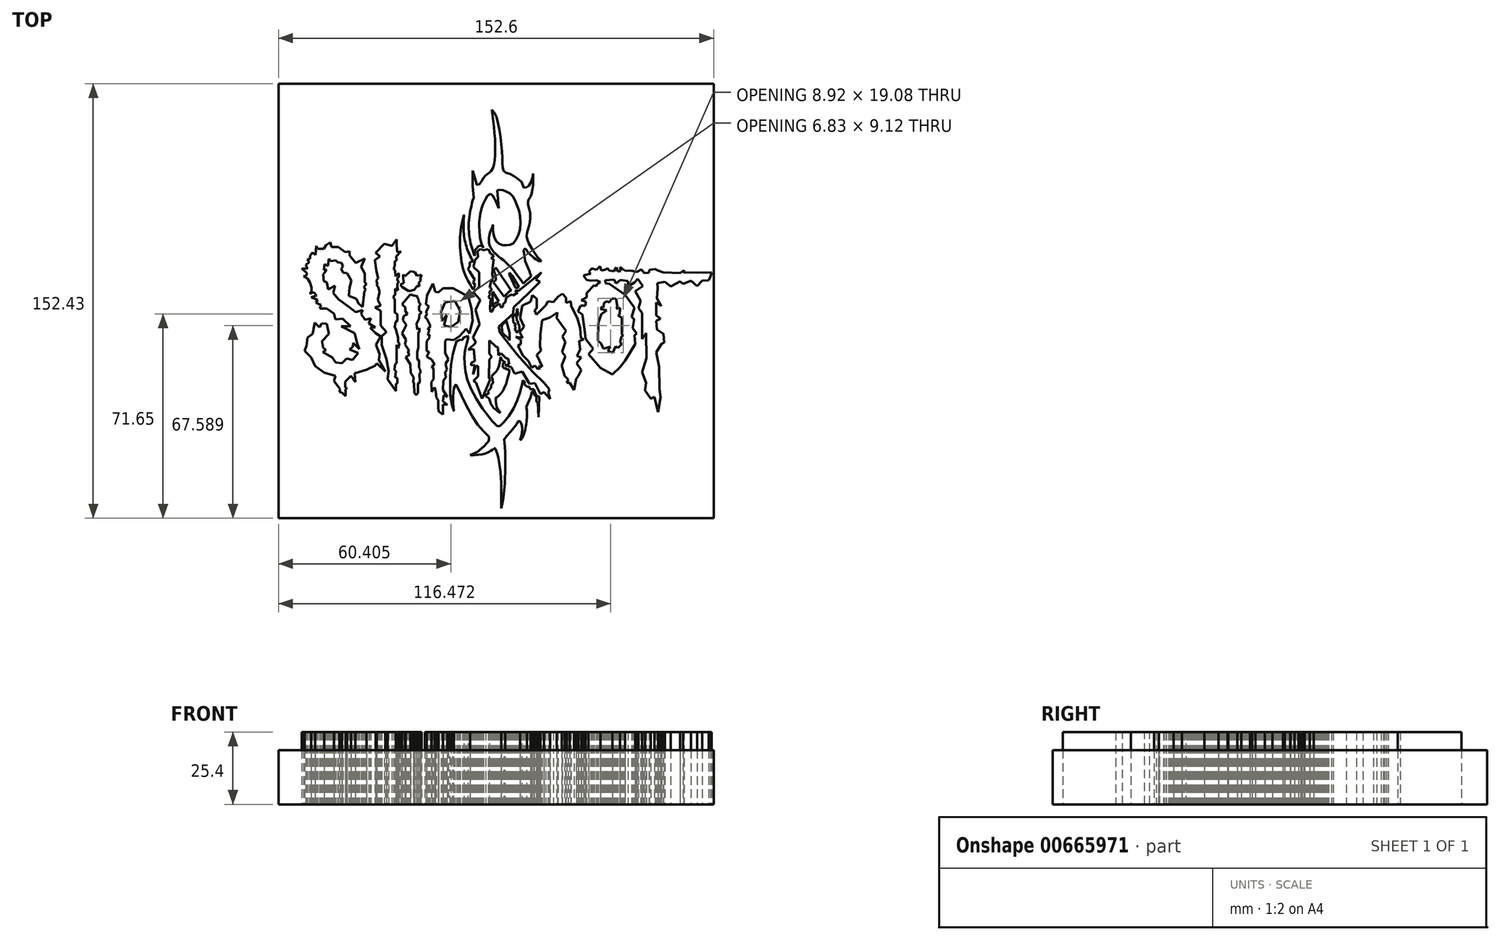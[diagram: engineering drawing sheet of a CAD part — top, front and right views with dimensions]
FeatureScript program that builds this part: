
annotation { "Feature Type Name" : "Feature", "Feature Type Description" : "" }
export const myFeature = defineFeature(function(context is Context, id is Id, definition is map)
    precondition{}
    {
        {
            var Q0;
            Q0=qCreatedBy(makeId("Top.planeOp"),FACE);
            var sketch = newSketch(context, id + "F0", { "sketchPlane" : qUnion([Q0])});
            skLineSegment(sketch, "E0", {"start": v(-46.73, -2.2) * mm, "end": v(-46.31, 1.77) * mm});
            skLineSegment(sketch, "E1", {"start": v(-46.31, 1.77) * mm, "end": v(-46.14, 3.42) * mm});
            skLineSegment(sketch, "E2", {"start": v(-46.14, 3.42) * mm, "end": v(-45.53, 4.04) * mm});
            skLineSegment(sketch, "E3", {"start": v(-45.53, 4.04) * mm, "end": v(-46.31, 4.8) * mm});
            skLineSegment(sketch, "E4", {"start": v(-46.31, 4.8) * mm, "end": v(-45.34, 6) * mm});
            skLineSegment(sketch, "E5", {"start": v(-45.34, 6) * mm, "end": v(-45.93, 6.49) * mm});
            skLineSegment(sketch, "E6", {"start": v(-45.93, 6.49) * mm, "end": v(-45.93, 9.65) * mm});
            skLineSegment(sketch, "E7", {"start": v(-45.93, 9.65) * mm, "end": v(-47.23, 11.97) * mm});
            skLineSegment(sketch, "E8", {"start": v(-47.23, 11.97) * mm, "end": v(-45.93, 14.84) * mm});
            skLineSegment(sketch, "E9", {"start": v(-45.93, 14.84) * mm, "end": v(-49.1, 13.34) * mm});
            skLineSegment(sketch, "E10", {"start": v(-49.1, 13.34) * mm, "end": v(-51.32, 15.98) * mm});
            skLineSegment(sketch, "E11", {"start": v(-51.32, 15.98) * mm, "end": v(-51.32, 17.42) * mm});
            skLineSegment(sketch, "E12", {"start": v(-51.32, 17.42) * mm, "end": v(-52.82, 17.15) * mm});
            skLineSegment(sketch, "E13", {"start": v(-52.82, 17.15) * mm, "end": v(-55.25, 18.95) * mm});
            skLineSegment(sketch, "E14", {"start": v(-55.25, 18.95) * mm, "end": v(-57.6, 18.95) * mm});
            skLineSegment(sketch, "E15", {"start": v(-57.6, 18.95) * mm, "end": v(-58.07, 20.52) * mm});
            skLineSegment(sketch, "E16", {"start": v(-58.07, 20.52) * mm, "end": v(-59.58, 19.6) * mm});
            skLineSegment(sketch, "E17", {"start": v(-59.58, 19.6) * mm, "end": v(-60.29, 18.29) * mm});
            skLineSegment(sketch, "E18", {"start": v(-60.29, 18.29) * mm, "end": v(-62.45, 18.29) * mm});
            skLineSegment(sketch, "E19", {"start": v(-62.45, 18.29) * mm, "end": v(-62.95, 19.34) * mm});
            skLineSegment(sketch, "E20", {"start": v(-62.95, 19.34) * mm, "end": v(-63.28, 16.19) * mm});
            skLineSegment(sketch, "E21", {"start": v(-63.28, 16.19) * mm, "end": v(-64.22, 16.97) * mm});
            skLineSegment(sketch, "E22", {"start": v(-64.22, 16.97) * mm, "end": v(-65.1, 15.9) * mm});
            skLineSegment(sketch, "E23", {"start": v(-65.1, 15.9) * mm, "end": v(-65.1, 14.84) * mm});
            skLineSegment(sketch, "E24", {"start": v(-65.1, 14.84) * mm, "end": v(-66.17, 14.48) * mm});
            skLineSegment(sketch, "E25", {"start": v(-66.17, 14.48) * mm, "end": v(-65.37, 13.68) * mm});
            skLineSegment(sketch, "E26", {"start": v(-65.37, 13.68) * mm, "end": v(-66.7, 12.59) * mm});
            skLineSegment(sketch, "E27", {"start": v(-66.7, 12.59) * mm, "end": v(-66.08, 11.26) * mm});
            skLineSegment(sketch, "E28", {"start": v(-66.08, 11.26) * mm, "end": v(-68.08, 11.47) * mm});
            skLineSegment(sketch, "E29", {"start": v(-68.08, 11.47) * mm, "end": v(-66.33, 9.83) * mm});
            skLineSegment(sketch, "E30", {"start": v(-66.33, 9.83) * mm, "end": v(-66.44, 8.84) * mm});
            skLineSegment(sketch, "E31", {"start": v(-66.44, 8.84) * mm, "end": v(-67.43, 8.67) * mm});
            skLineSegment(sketch, "E32", {"start": v(-67.43, 8.67) * mm, "end": v(-66.06, 7.88) * mm});
            skLineSegment(sketch, "E33", {"start": v(-66.06, 7.88) * mm, "end": v(-65.18, 6.39) * mm});
            skLineSegment(sketch, "E34", {"start": v(-65.18, 6.39) * mm, "end": v(-64.68, 4.65) * mm});
            skLineSegment(sketch, "E35", {"start": v(-64.68, 4.65) * mm, "end": v(-64.68, 3.48) * mm});
            skLineSegment(sketch, "E36", {"start": v(-64.68, 3.48) * mm, "end": v(-65.23, 2.52) * mm});
            skLineSegment(sketch, "E37", {"start": v(-65.23, 2.52) * mm, "end": v(-63.86, 3.09) * mm});
            skLineSegment(sketch, "E38", {"start": v(-63.86, 3.09) * mm, "end": v(-62.82, 1.92) * mm});
            skLineSegment(sketch, "E39", {"start": v(-62.82, 1.92) * mm, "end": v(-64.73, 1.23) * mm});
            skLineSegment(sketch, "E40", {"start": v(-64.73, 1.23) * mm, "end": v(-62.52, 0.39) * mm});
            skLineSegment(sketch, "E41", {"start": v(-62.52, 0.39) * mm, "end": v(-63.09, -0.6) * mm});
            skLineSegment(sketch, "E42", {"start": v(-63.09, -0.6) * mm, "end": v(-61.3, -1.37) * mm});
            skLineSegment(sketch, "E43", {"start": v(-61.3, -1.37) * mm, "end": v(-61.7, -2.69) * mm});
            skLineSegment(sketch, "E44", {"start": v(-61.7, -2.69) * mm, "end": v(-59.24, -2.69) * mm});
            skLineSegment(sketch, "E45", {"start": v(-59.24, -2.69) * mm, "end": v(-56.72, -4.4) * mm});
            skLineSegment(sketch, "E46", {"start": v(-56.72, -4.4) * mm, "end": v(-56.2, -6.44) * mm});
            skLineSegment(sketch, "E47", {"start": v(-56.2, -6.44) * mm, "end": v(-53.75, -6.25) * mm});
            skLineSegment(sketch, "E48", {"start": v(-53.75, -6.25) * mm, "end": v(-50.94, -8.88) * mm});
            skLineSegment(sketch, "E49", {"start": v(-50.94, -8.88) * mm, "end": v(-54.27, -8.88) * mm});
            skLineSegment(sketch, "E50", {"start": v(-54.27, -8.88) * mm, "end": v(-49.54, -11.25) * mm});
            skLineSegment(sketch, "E51", {"start": v(-49.54, -11.25) * mm, "end": v(-48.66, -14.88) * mm});
            skLineSegment(sketch, "E52", {"start": v(-48.66, -14.88) * mm, "end": v(-47.82, -16.95) * mm});
            skLineSegment(sketch, "E53", {"start": v(-47.82, -16.95) * mm, "end": v(-50.04, -14.74) * mm});
            skLineSegment(sketch, "E54", {"start": v(-50.04, -14.74) * mm, "end": v(-50.1, -16.14) * mm});
            skLineSegment(sketch, "E55", {"start": v(-50.1, -16.14) * mm, "end": v(-51.34, -16.98) * mm});
            skLineSegment(sketch, "E56", {"start": v(-51.34, -16.98) * mm, "end": v(-48.2, -18.25) * mm});
            skLineSegment(sketch, "E57", {"start": v(-48.2, -18.25) * mm, "end": v(-50.28, -20.65) * mm});
            skLineSegment(sketch, "E58", {"start": v(-50.28, -20.65) * mm, "end": v(-52.31, -20.2) * mm});
            skLineSegment(sketch, "E59", {"start": v(-52.31, -20.2) * mm, "end": v(-53.9, -21.8) * mm});
            skLineSegment(sketch, "E60", {"start": v(-53.9, -21.8) * mm, "end": v(-56.13, -21.54) * mm});
            skLineSegment(sketch, "E61", {"start": v(-56.13, -21.54) * mm, "end": v(-57.38, -19.8) * mm});
            skLineSegment(sketch, "E62", {"start": v(-57.38, -19.8) * mm, "end": v(-60.63, -17.93) * mm});
            skLineSegment(sketch, "E63", {"start": v(-60.63, -17.93) * mm, "end": v(-59.6, -17.3) * mm});
            skLineSegment(sketch, "E64", {"start": v(-59.6, -17.3) * mm, "end": v(-60.55, -16.38) * mm});
            skLineSegment(sketch, "E65", {"start": v(-60.55, -16.38) * mm, "end": v(-60.95, -14.13) * mm});
            skLineSegment(sketch, "E66", {"start": v(-60.95, -14.13) * mm, "end": v(-58.48, -11.6) * mm});
            skLineSegment(sketch, "E67", {"start": v(-58.48, -11.6) * mm, "end": v(-59.24, -7.98) * mm});
            skLineSegment(sketch, "E68", {"start": v(-59.24, -7.98) * mm, "end": v(-61.08, -7.88) * mm});
            skLineSegment(sketch, "E69", {"start": v(-61.08, -7.88) * mm, "end": v(-61.85, -9.23) * mm});
            skLineSegment(sketch, "E70", {"start": v(-61.85, -9.23) * mm, "end": v(-63.46, -7.66) * mm});
            skLineSegment(sketch, "E71", {"start": v(-63.46, -7.66) * mm, "end": v(-64.2, -11.53) * mm});
            skLineSegment(sketch, "E72", {"start": v(-64.2, -11.53) * mm, "end": v(-66.06, -12.87) * mm});
            skLineSegment(sketch, "E73", {"start": v(-66.06, -12.87) * mm, "end": v(-66.38, -15.81) * mm});
            skLineSegment(sketch, "E74", {"start": v(-66.38, -15.81) * mm, "end": v(-67.09, -17.55) * mm});
            skLineSegment(sketch, "E75", {"start": v(-67.09, -17.55) * mm, "end": v(-64.78, -19.8) * mm});
            skLineSegment(sketch, "E76", {"start": v(-64.78, -19.8) * mm, "end": v(-63.41, -22.83) * mm});
            skLineSegment(sketch, "E77", {"start": v(-63.41, -22.83) * mm, "end": v(-60.23, -25.2) * mm});
            skLineSegment(sketch, "E78", {"start": v(-60.23, -25.2) * mm, "end": v(-56.24, -26.28) * mm});
            skLineSegment(sketch, "E79", {"start": v(-56.24, -26.28) * mm, "end": v(-56.72, -28.03) * mm});
            skLineSegment(sketch, "E80", {"start": v(-56.72, -28.03) * mm, "end": v(-55.48, -29.75) * mm});
            skLineSegment(sketch, "E81", {"start": v(-55.48, -29.75) * mm, "end": v(-54.57, -31.02) * mm});
            skLineSegment(sketch, "E82", {"start": v(-54.57, -31.02) * mm, "end": v(-54.83, -31.95) * mm});
            skLineSegment(sketch, "E83", {"start": v(-54.83, -31.95) * mm, "end": v(-54, -32.17) * mm});
            skLineSegment(sketch, "E84", {"start": v(-54, -32.17) * mm, "end": v(-52.71, -33.43) * mm});
            skLineSegment(sketch, "E85", {"start": v(-52.71, -33.43) * mm, "end": v(-52.71, -31.02) * mm});
            skLineSegment(sketch, "E86", {"start": v(-52.71, -31.02) * mm, "end": v(-52.2, -30.65) * mm});
            skLineSegment(sketch, "E87", {"start": v(-52.2, -30.65) * mm, "end": v(-52.76, -30.4) * mm});
            skLineSegment(sketch, "E88", {"start": v(-52.76, -30.4) * mm, "end": v(-52.76, -28.3) * mm});
            skLineSegment(sketch, "E89", {"start": v(-52.76, -28.3) * mm, "end": v(-50.84, -26.31) * mm});
            skLineSegment(sketch, "E90", {"start": v(-50.84, -26.31) * mm, "end": v(-49.3, -28.47) * mm});
            skLineSegment(sketch, "E91", {"start": v(-49.3, -28.47) * mm, "end": v(-49.54, -25.35) * mm});
            skLineSegment(sketch, "E92", {"start": v(-49.54, -25.35) * mm, "end": v(-45.32, -24.15) * mm});
            skLineSegment(sketch, "E93", {"start": v(-45.32, -24.15) * mm, "end": v(-42.11, -22.56) * mm});
            skLineSegment(sketch, "E94", {"start": v(-42.11, -22.56) * mm, "end": v(-41.72, -21.88) * mm});
            skLineSegment(sketch, "E95", {"start": v(-41.72, -21.88) * mm, "end": v(-38.71, -24.8) * mm});
            skLineSegment(sketch, "E96", {"start": v(-38.71, -24.8) * mm, "end": v(-41, -20.64) * mm});
            skLineSegment(sketch, "E97", {"start": v(-41, -20.64) * mm, "end": v(-40.71, -18.7) * mm});
            skLineSegment(sketch, "E98", {"start": v(-40.71, -18.7) * mm, "end": v(-42.02, -15.33) * mm});
            skLineSegment(sketch, "E99", {"start": v(-42.02, -15.33) * mm, "end": v(-40.34, -12.4) * mm});
            skLineSegment(sketch, "E100", {"start": v(-40.34, -12.4) * mm, "end": v(-42.08, -11.25) * mm});
            skLineSegment(sketch, "E101", {"start": v(-42.08, -11.25) * mm, "end": v(-44.01, -9.36) * mm});
            skLineSegment(sketch, "E102", {"start": v(-44.01, -9.36) * mm, "end": v(-42.32, -9.21) * mm});
            skLineSegment(sketch, "E103", {"start": v(-42.32, -9.21) * mm, "end": v(-44.6, -7.9) * mm});
            skLineSegment(sketch, "E104", {"start": v(-44.6, -7.9) * mm, "end": v(-43.86, -6.08) * mm});
            skLineSegment(sketch, "E105", {"start": v(-43.86, -6.08) * mm, "end": v(-45.78, -6.6) * mm});
            skLineSegment(sketch, "E106", {"start": v(-45.78, -6.6) * mm, "end": v(-47.27, -4.53) * mm});
            skLineSegment(sketch, "E107", {"start": v(-47.27, -4.53) * mm, "end": v(-46.72, -3.17) * mm});
            skLineSegment(sketch, "E108", {"start": v(-46.72, -3.17) * mm, "end": v(-49.14, -3.92) * mm});
            skLineSegment(sketch, "E109", {"start": v(-49.14, -3.92) * mm, "end": v(-51.42, -2.14) * mm});
            skLineSegment(sketch, "E110", {"start": v(-51.42, -2.14) * mm, "end": v(-55.25, 0.63) * mm});
            skLineSegment(sketch, "E111", {"start": v(-55.25, 0.63) * mm, "end": v(-57.06, 2.73) * mm});
            skLineSegment(sketch, "E112", {"start": v(-57.06, 2.73) * mm, "end": v(-56.34, 5.4) * mm});
            skLineSegment(sketch, "E113", {"start": v(-56.34, 5.4) * mm, "end": v(-58.78, 4.1) * mm});
            skLineSegment(sketch, "E114", {"start": v(-58.78, 4.1) * mm, "end": v(-59.24, 6.57) * mm});
            skLineSegment(sketch, "E115", {"start": v(-59.24, 6.57) * mm, "end": v(-60.3, 6.86) * mm});
            skLineSegment(sketch, "E116", {"start": v(-60.3, 6.86) * mm, "end": v(-60.55, 9.24) * mm});
            skLineSegment(sketch, "E117", {"start": v(-60.55, 9.24) * mm, "end": v(-59.24, 10.93) * mm});
            skLineSegment(sketch, "E118", {"start": v(-59.24, 10.93) * mm, "end": v(-60.35, 10.93) * mm});
            skLineSegment(sketch, "E119", {"start": v(-60.35, 10.93) * mm, "end": v(-60.04, 13) * mm});
            skLineSegment(sketch, "E120", {"start": v(-60.04, 13) * mm, "end": v(-58.9, 12.25) * mm});
            skLineSegment(sketch, "E121", {"start": v(-58.9, 12.25) * mm, "end": v(-58.52, 14.8) * mm});
            skLineSegment(sketch, "E122", {"start": v(-58.52, 14.8) * mm, "end": v(-57.95, 14.01) * mm});
            skLineSegment(sketch, "E123", {"start": v(-57.95, 14.01) * mm, "end": v(-56.17, 14.27) * mm});
            skLineSegment(sketch, "E124", {"start": v(-56.17, 14.27) * mm, "end": v(-55.48, 13.6) * mm});
            skLineSegment(sketch, "E125", {"start": v(-55.48, 13.6) * mm, "end": v(-54.05, 13.38) * mm});
            skLineSegment(sketch, "E126", {"start": v(-54.05, 13.38) * mm, "end": v(-53.52, 12) * mm});
            skLineSegment(sketch, "E127", {"start": v(-53.52, 12) * mm, "end": v(-54.26, 11.24) * mm});
            skLineSegment(sketch, "E128", {"start": v(-54.26, 11.24) * mm, "end": v(-53.56, 9.96) * mm});
            skLineSegment(sketch, "E129", {"start": v(-53.56, 9.96) * mm, "end": v(-52.22, 9.76) * mm});
            skLineSegment(sketch, "E130", {"start": v(-52.22, 9.76) * mm, "end": v(-50.7, 7.1) * mm});
            skLineSegment(sketch, "E131", {"start": v(-50.7, 7.1) * mm, "end": v(-51.33, 4.74) * mm});
            skLineSegment(sketch, "E132", {"start": v(-51.33, 4.74) * mm, "end": v(-51.48, 1.75) * mm});
            skLineSegment(sketch, "E133", {"start": v(-51.48, 1.75) * mm, "end": v(-48.93, 0.71) * mm});
            skLineSegment(sketch, "E134", {"start": v(-48.93, 0.71) * mm, "end": v(-48.21, -0.75) * mm});
            skLineSegment(sketch, "E135", {"start": v(-48.21, -0.75) * mm, "end": v(-46.73, -2.2) * mm});
            skPoint(sketch, "E136.end.orphan", {"position": v(-38.71, 15.6) * mm});
            skLineSegment(sketch, "E137", {"start": v(-34.72, 21.53) * mm, "end": v(-36.49, 19.25) * mm});
            skLineSegment(sketch, "E138", {"start": v(-36.49, 19.25) * mm, "end": v(-39.07, 20.12) * mm});
            skLineSegment(sketch, "E139", {"start": v(-39.07, 20.12) * mm, "end": v(-42.1, 16.94) * mm});
            skLineSegment(sketch, "E140", {"start": v(-42.1, 16.94) * mm, "end": v(-40.65, 15.57) * mm});
            skLineSegment(sketch, "E141", {"start": v(-40.65, 15.57) * mm, "end": v(-42.37, 14.39) * mm});
            skLineSegment(sketch, "E142", {"start": v(-42.37, 14.39) * mm, "end": v(-41.93, 10.72) * mm});
            skLineSegment(sketch, "E143", {"start": v(-41.93, 10.72) * mm, "end": v(-41.3, 7.92) * mm});
            skLineSegment(sketch, "E144", {"start": v(-41.3, 7.92) * mm, "end": v(-42.03, 6.97) * mm});
            skLineSegment(sketch, "E145", {"start": v(-42.03, 6.97) * mm, "end": v(-41.32, 6.12) * mm});
            skLineSegment(sketch, "E146", {"start": v(-41.32, 6.12) * mm, "end": v(-41.83, 5.7) * mm});
            skLineSegment(sketch, "E147", {"start": v(-41.83, 5.7) * mm, "end": v(-41.19, 4.93) * mm});
            skLineSegment(sketch, "E148", {"start": v(-41.19, 4.93) * mm, "end": v(-40.71, 3.12) * mm});
            skLineSegment(sketch, "E149", {"start": v(-40.71, 3.12) * mm, "end": v(-41.4, 0.32) * mm});
            skLineSegment(sketch, "E150", {"start": v(-41.4, 0.32) * mm, "end": v(-40.32, -1.68) * mm});
            skLineSegment(sketch, "E151", {"start": v(-40.32, -1.68) * mm, "end": v(-42.44, -2.34) * mm});
            skLineSegment(sketch, "E152", {"start": v(-42.44, -2.34) * mm, "end": v(-40.32, -3.44) * mm});
            skLineSegment(sketch, "E153", {"start": v(-40.32, -3.44) * mm, "end": v(-40.32, -8.64) * mm});
            skLineSegment(sketch, "E154", {"start": v(-40.32, -8.64) * mm, "end": v(-38.29, -10.9) * mm});
            skLineSegment(sketch, "E155", {"start": v(-38.29, -10.9) * mm, "end": v(-39.92, -12.36) * mm});
            skLineSegment(sketch, "E156", {"start": v(-39.92, -12.36) * mm, "end": v(-39.92, -15.52) * mm});
            skLineSegment(sketch, "E157", {"start": v(-39.92, -15.52) * mm, "end": v(-38.33, -20.4) * mm});
            skLineSegment(sketch, "E158", {"start": v(-38.33, -20.4) * mm, "end": v(-37.61, -24.6) * mm});
            skLineSegment(sketch, "E159", {"start": v(-37.61, -24.6) * mm, "end": v(-37.89, -27.38) * mm});
            skLineSegment(sketch, "E160", {"start": v(-37.89, -27.38) * mm, "end": v(-35, -31.58) * mm});
            skLineSegment(sketch, "E161", {"start": v(-35, -31.58) * mm, "end": v(-35, -29.16) * mm});
            skLineSegment(sketch, "E162", {"start": v(-35, -29.16) * mm, "end": v(-34.46, -28.86) * mm});
            skLineSegment(sketch, "E163", {"start": v(-34.46, -28.86) * mm, "end": v(-34.46, -27.04) * mm});
            skLineSegment(sketch, "E164", {"start": v(-34.46, -27.04) * mm, "end": v(-35.21, -26.85) * mm});
            skLineSegment(sketch, "E165", {"start": v(-35.21, -26.85) * mm, "end": v(-34.99, -24.58) * mm});
            skLineSegment(sketch, "E166", {"start": v(-34.99, -24.58) * mm, "end": v(-35.49, -24.1) * mm});
            skLineSegment(sketch, "E167", {"start": v(-35.49, -24.1) * mm, "end": v(-35.3, -22.1) * mm});
            skLineSegment(sketch, "E168", {"start": v(-35.3, -22.1) * mm, "end": v(-34.76, -21.8) * mm});
            skLineSegment(sketch, "E169", {"start": v(-34.76, -21.8) * mm, "end": v(-34.76, -15.73) * mm});
            skLineSegment(sketch, "E170", {"start": v(-34.76, -15.73) * mm, "end": v(-34.66, -15.3) * mm});
            skLineSegment(sketch, "E171", {"start": v(-34.66, -15.3) * mm, "end": v(-34.26, -16.66) * mm});
            skLineSegment(sketch, "E172", {"start": v(-34.26, -16.66) * mm, "end": v(-33.8, -14.86) * mm});
            skLineSegment(sketch, "E173", {"start": v(-33.8, -14.86) * mm, "end": v(-34.32, -14.46) * mm});
            skLineSegment(sketch, "E174", {"start": v(-34.32, -14.46) * mm, "end": v(-34.32, -12.85) * mm});
            skLineSegment(sketch, "E175", {"start": v(-34.32, -12.85) * mm, "end": v(-35.04, -10.03) * mm});
            skLineSegment(sketch, "E176", {"start": v(-35.04, -10.03) * mm, "end": v(-35.38, -9.18) * mm});
            skLineSegment(sketch, "E177", {"start": v(-35.38, -9.18) * mm, "end": v(-35.2, -7.33) * mm});
            skLineSegment(sketch, "E178", {"start": v(-35.2, -7.33) * mm, "end": v(-34.58, -7.03) * mm});
            skLineSegment(sketch, "E179", {"start": v(-34.58, -7.03) * mm, "end": v(-34.58, -4.68) * mm});
            skLineSegment(sketch, "E180", {"start": v(-34.58, -4.68) * mm, "end": v(-35.45, -4.1) * mm});
            skLineSegment(sketch, "E181", {"start": v(-35.45, -4.1) * mm, "end": v(-35.45, 0.62) * mm});
            skLineSegment(sketch, "E182", {"start": v(-35.45, 0.62) * mm, "end": v(-35.82, 0.88) * mm});
            skLineSegment(sketch, "E183", {"start": v(-35.82, 0.88) * mm, "end": v(-35.77, 1.82) * mm});
            skLineSegment(sketch, "E184", {"start": v(-35.77, 1.82) * mm, "end": v(-35.34, 2.15) * mm});
            skLineSegment(sketch, "E185", {"start": v(-35.34, 2.15) * mm, "end": v(-35.34, 4.27) * mm});
            skLineSegment(sketch, "E186", {"start": v(-35.34, 4.27) * mm, "end": v(-34.29, 3.72) * mm});
            skLineSegment(sketch, "E187", {"start": v(-34.29, 3.72) * mm, "end": v(-34.58, 4.93) * mm});
            skLineSegment(sketch, "E188", {"start": v(-34.58, 4.93) * mm, "end": v(-34.58, 6.14) * mm});
            skLineSegment(sketch, "E189", {"start": v(-34.58, 6.14) * mm, "end": v(-34.18, 6.53) * mm});
            skLineSegment(sketch, "E190", {"start": v(-34.18, 6.53) * mm, "end": v(-34.04, 7) * mm});
            skLineSegment(sketch, "E191", {"start": v(-34.04, 7) * mm, "end": v(-34.58, 7.05) * mm});
            skLineSegment(sketch, "E192", {"start": v(-34.58, 7.05) * mm, "end": v(-34.58, 8.05) * mm});
            skLineSegment(sketch, "E193", {"start": v(-34.58, 8.05) * mm, "end": v(-33.96, 8.32) * mm});
            skLineSegment(sketch, "E194", {"start": v(-33.96, 8.32) * mm, "end": v(-33.96, 9.83) * mm});
            skLineSegment(sketch, "E195", {"start": v(-33.96, 9.83) * mm, "end": v(-35.1, 8.66) * mm});
            skLineSegment(sketch, "E196", {"start": v(-35.1, 8.66) * mm, "end": v(-35.32, 10.67) * mm});
            skLineSegment(sketch, "E197", {"start": v(-35.32, 10.67) * mm, "end": v(-35.71, 10.94) * mm});
            skLineSegment(sketch, "E198", {"start": v(-35.71, 10.94) * mm, "end": v(-35.71, 11.88) * mm});
            skLineSegment(sketch, "E199", {"start": v(-35.71, 11.88) * mm, "end": v(-35.4, 12.15) * mm});
            skLineSegment(sketch, "E200", {"start": v(-35.4, 12.15) * mm, "end": v(-35.4, 13.97) * mm});
            skLineSegment(sketch, "E201", {"start": v(-35.4, 13.97) * mm, "end": v(-34.82, 14.28) * mm});
            skLineSegment(sketch, "E202", {"start": v(-34.82, 14.28) * mm, "end": v(-34.9, 15.6) * mm});
            skLineSegment(sketch, "E203", {"start": v(-34.9, 15.6) * mm, "end": v(-33.23, 17.41) * mm});
            skLineSegment(sketch, "E204", {"start": v(-33.23, 17.41) * mm, "end": v(-34.58, 17.08) * mm});
            skLineSegment(sketch, "E205", {"start": v(-34.58, 17.08) * mm, "end": v(-34.77, 19.41) * mm});
            skLineSegment(sketch, "E206", {"start": v(-34.77, 19.41) * mm, "end": v(-34.72, 21.53) * mm});
            skLineSegment(sketch, "E207", {"start": v(-29.97, 10.44) * mm, "end": v(-31.9, 8.58) * mm});
            skLineSegment(sketch, "E208", {"start": v(-31.9, 8.58) * mm, "end": v(-32.52, 9.22) * mm});
            skLineSegment(sketch, "E209", {"start": v(-32.52, 9.22) * mm, "end": v(-32.52, 7.9) * mm});
            skLineSegment(sketch, "E210", {"start": v(-32.52, 7.9) * mm, "end": v(-32.24, 6.37) * mm});
            skLineSegment(sketch, "E211", {"start": v(-32.24, 6.37) * mm, "end": v(-33.5, 5.68) * mm});
            skLineSegment(sketch, "E212", {"start": v(-33.5, 5.68) * mm, "end": v(-32.7, 4.8) * mm});
            skLineSegment(sketch, "E213", {"start": v(-32.7, 4.8) * mm, "end": v(-30.48, 3.44) * mm});
            skLineSegment(sketch, "E214", {"start": v(-30.48, 3.44) * mm, "end": v(-28.61, 3.98) * mm});
            skLineSegment(sketch, "E215", {"start": v(-28.61, 3.98) * mm, "end": v(-27.51, 5.39) * mm});
            skLineSegment(sketch, "E216", {"start": v(-27.51, 5.39) * mm, "end": v(-26.72, 5.08) * mm});
            skLineSegment(sketch, "E217", {"start": v(-26.72, 5.08) * mm, "end": v(-27.06, 6.5) * mm});
            skLineSegment(sketch, "E218", {"start": v(-27.06, 6.5) * mm, "end": v(-26.32, 7.16) * mm});
            skLineSegment(sketch, "E219", {"start": v(-26.32, 7.16) * mm, "end": v(-26.51, 7.8) * mm});
            skLineSegment(sketch, "E220", {"start": v(-26.51, 7.8) * mm, "end": v(-26, 9.09) * mm});
            skLineSegment(sketch, "E221", {"start": v(-26, 9.09) * mm, "end": v(-27.72, 8.83) * mm});
            skLineSegment(sketch, "E222", {"start": v(-27.72, 8.83) * mm, "end": v(-28.41, 10.1) * mm});
            skLineSegment(sketch, "E223", {"start": v(-28.41, 10.1) * mm, "end": v(-29.97, 10.44) * mm});
            skLineSegment(sketch, "E224", {"start": v(-29.97, 2.3) * mm, "end": v(-32.85, -1.12) * mm});
            skLineSegment(sketch, "E225", {"start": v(-32.85, -1.12) * mm, "end": v(-31.6, -2.47) * mm});
            skLineSegment(sketch, "E226", {"start": v(-31.6, -2.47) * mm, "end": v(-31.83, -3.3) * mm});
            skLineSegment(sketch, "E227", {"start": v(-31.83, -3.3) * mm, "end": v(-30.92, -4.74) * mm});
            skLineSegment(sketch, "E228", {"start": v(-30.92, -4.74) * mm, "end": v(-32.17, -5.23) * mm});
            skLineSegment(sketch, "E229", {"start": v(-32.17, -5.23) * mm, "end": v(-32.56, -6.72) * mm});
            skLineSegment(sketch, "E230", {"start": v(-32.56, -6.72) * mm, "end": v(-31.37, -8.4) * mm});
            skLineSegment(sketch, "E231", {"start": v(-31.37, -8.4) * mm, "end": v(-32.85, -11.38) * mm});
            skLineSegment(sketch, "E232", {"start": v(-32.85, -11.38) * mm, "end": v(-31.41, -13.63) * mm});
            skLineSegment(sketch, "E233", {"start": v(-31.41, -13.63) * mm, "end": v(-31.81, -15.26) * mm});
            skLineSegment(sketch, "E234", {"start": v(-31.81, -15.26) * mm, "end": v(-30.82, -16.75) * mm});
            skLineSegment(sketch, "E235", {"start": v(-30.82, -16.75) * mm, "end": v(-30.29, -17.58) * mm});
            skLineSegment(sketch, "E236", {"start": v(-30.29, -17.58) * mm, "end": v(-31, -17.85) * mm});
            skLineSegment(sketch, "E237", {"start": v(-31, -17.85) * mm, "end": v(-30.24, -18.95) * mm});
            skLineSegment(sketch, "E238", {"start": v(-30.24, -18.95) * mm, "end": v(-31.6, -19.7) * mm});
            skLineSegment(sketch, "E239", {"start": v(-31.6, -19.7) * mm, "end": v(-29.91, -22.25) * mm});
            skLineSegment(sketch, "E240", {"start": v(-29.91, -22.25) * mm, "end": v(-29.86, -25.23) * mm});
            skLineSegment(sketch, "E241", {"start": v(-29.86, -25.23) * mm, "end": v(-28.86, -26.77) * mm});
            skLineSegment(sketch, "E242", {"start": v(-28.86, -26.77) * mm, "end": v(-28.95, -28.39) * mm});
            skLineSegment(sketch, "E243", {"start": v(-28.95, -28.39) * mm, "end": v(-28.63, -29.02) * mm});
            skLineSegment(sketch, "E244", {"start": v(-28.63, -29.02) * mm, "end": v(-28.61, -32.27) * mm});
            skLineSegment(sketch, "E245", {"start": v(-28.61, -32.27) * mm, "end": v(-27.86, -32.98) * mm});
            skLineSegment(sketch, "E246", {"start": v(-27.86, -32.98) * mm, "end": v(-27.24, -32.3) * mm});
            skLineSegment(sketch, "E247", {"start": v(-27.24, -32.3) * mm, "end": v(-27.35, -28.9) * mm});
            skLineSegment(sketch, "E248", {"start": v(-27.35, -28.9) * mm, "end": v(-26.7, -28.54) * mm});
            skLineSegment(sketch, "E249", {"start": v(-26.7, -28.54) * mm, "end": v(-26.84, -25.48) * mm});
            skLineSegment(sketch, "E250", {"start": v(-26.84, -25.48) * mm, "end": v(-26.45, -25.14) * mm});
            skLineSegment(sketch, "E251", {"start": v(-26.45, -25.14) * mm, "end": v(-26.5, -24) * mm});
            skLineSegment(sketch, "E252", {"start": v(-26.5, -24) * mm, "end": v(-26.94, -23.5) * mm});
            skLineSegment(sketch, "E253", {"start": v(-26.94, -23.5) * mm, "end": v(-26.88, -20.83) * mm});
            skLineSegment(sketch, "E254", {"start": v(-26.88, -20.83) * mm, "end": v(-27.59, -20.43) * mm});
            skLineSegment(sketch, "E255", {"start": v(-27.59, -20.43) * mm, "end": v(-27.48, -17.9) * mm});
            skLineSegment(sketch, "E256", {"start": v(-27.48, -17.9) * mm, "end": v(-27.15, -16.33) * mm});
            skLineSegment(sketch, "E257", {"start": v(-27.15, -16.33) * mm, "end": v(-27.21, -13.78) * mm});
            skLineSegment(sketch, "E258", {"start": v(-27.21, -13.78) * mm, "end": v(-27.21, -11.47) * mm});
            skLineSegment(sketch, "E259", {"start": v(-27.21, -11.47) * mm, "end": v(-26.8, -10.54) * mm});
            skLineSegment(sketch, "E260", {"start": v(-26.8, -10.54) * mm, "end": v(-26.82, -9.58) * mm});
            skLineSegment(sketch, "E261", {"start": v(-26.82, -9.58) * mm, "end": v(-27.56, -10) * mm});
            skLineSegment(sketch, "E262", {"start": v(-27.56, -10) * mm, "end": v(-27.81, -7.96) * mm});
            skLineSegment(sketch, "E263", {"start": v(-27.81, -7.96) * mm, "end": v(-26.87, -6.21) * mm});
            skLineSegment(sketch, "E264", {"start": v(-26.87, -6.21) * mm, "end": v(-26.82, -4.7) * mm});
            skLineSegment(sketch, "E265", {"start": v(-26.82, -4.7) * mm, "end": v(-26.02, -4.02) * mm});
            skLineSegment(sketch, "E266", {"start": v(-26.02, -4.02) * mm, "end": v(-26.95, -3.36) * mm});
            skLineSegment(sketch, "E267", {"start": v(-26.95, -3.36) * mm, "end": v(-26.95, -1.83) * mm});
            skLineSegment(sketch, "E268", {"start": v(-26.95, -1.83) * mm, "end": v(-26.42, -1.46) * mm});
            skLineSegment(sketch, "E269", {"start": v(-26.42, -1.46) * mm, "end": v(-26.52, -0.91) * mm});
            skLineSegment(sketch, "E270", {"start": v(-26.52, -0.91) * mm, "end": v(-26.96, -0.76) * mm});
            skLineSegment(sketch, "E271", {"start": v(-26.96, -0.76) * mm, "end": v(-27.11, 0.7) * mm});
            skLineSegment(sketch, "E272", {"start": v(-27.11, 0.7) * mm, "end": v(-27.55, 1.04) * mm});
            skLineSegment(sketch, "E273", {"start": v(-27.55, 1.04) * mm, "end": v(-27.35, 1.63) * mm});
            skLineSegment(sketch, "E274", {"start": v(-27.35, 1.63) * mm, "end": v(-28.85, 1.96) * mm});
            skLineSegment(sketch, "E275", {"start": v(-28.85, 1.96) * mm, "end": v(-29.97, 2.3) * mm});
            skLineSegment(sketch, "E276", {"start": v(-22.02, 6.06) * mm, "end": v(-24.12, 1.92) * mm});
            skLineSegment(sketch, "E277", {"start": v(-24.12, 1.92) * mm, "end": v(-24.43, -1.17) * mm});
            skLineSegment(sketch, "E278", {"start": v(-24.43, -1.17) * mm, "end": v(-23.48, -1.88) * mm});
            skLineSegment(sketch, "E279", {"start": v(-23.48, -1.88) * mm, "end": v(-24.32, -3.66) * mm});
            skLineSegment(sketch, "E280", {"start": v(-24.32, -3.66) * mm, "end": v(-24.18, -5) * mm});
            skLineSegment(sketch, "E281", {"start": v(-24.18, -5) * mm, "end": v(-24.86, -5.6) * mm});
            skLineSegment(sketch, "E282", {"start": v(-24.86, -5.6) * mm, "end": v(-24.1, -6.4) * mm});
            skLineSegment(sketch, "E283", {"start": v(-24.1, -6.4) * mm, "end": v(-23.04, -8.34) * mm});
            skLineSegment(sketch, "E284", {"start": v(-23.04, -8.34) * mm, "end": v(-23.07, -9.38) * mm});
            skLineSegment(sketch, "E285", {"start": v(-23.07, -9.38) * mm, "end": v(-23.9, -9.53) * mm});
            skLineSegment(sketch, "E286", {"start": v(-23.9, -9.53) * mm, "end": v(-23.19, -10.57) * mm});
            skLineSegment(sketch, "E287", {"start": v(-23.19, -10.57) * mm, "end": v(-23.82, -11.3) * mm});
            skLineSegment(sketch, "E288", {"start": v(-23.82, -11.3) * mm, "end": v(-23.13, -12.6) * mm});
            skLineSegment(sketch, "E289", {"start": v(-23.13, -12.6) * mm, "end": v(-24.22, -14.21) * mm});
            skLineSegment(sketch, "E290", {"start": v(-24.22, -14.21) * mm, "end": v(-24.22, -17.7) * mm});
            skLineSegment(sketch, "E291", {"start": v(-24.22, -17.7) * mm, "end": v(-23.3, -17.78) * mm});
            skLineSegment(sketch, "E292", {"start": v(-23.3, -17.78) * mm, "end": v(-24.24, -19.56) * mm});
            skLineSegment(sketch, "E293", {"start": v(-24.24, -19.56) * mm, "end": v(-22.44, -20.6) * mm});
            skLineSegment(sketch, "E294", {"start": v(-22.44, -20.6) * mm, "end": v(-21.4, -22.32) * mm});
            skLineSegment(sketch, "E295", {"start": v(-21.4, -22.32) * mm, "end": v(-22.47, -22.88) * mm});
            skLineSegment(sketch, "E296", {"start": v(-22.47, -22.88) * mm, "end": v(-21.79, -23.83) * mm});
            skLineSegment(sketch, "E297", {"start": v(-21.79, -23.83) * mm, "end": v(-21.79, -27.38) * mm});
            skLineSegment(sketch, "E298", {"start": v(-21.79, -27.38) * mm, "end": v(-22.63, -28.46) * mm});
            skLineSegment(sketch, "E299", {"start": v(-22.63, -28.46) * mm, "end": v(-22.42, -31.9) * mm});
            skLineSegment(sketch, "E300", {"start": v(-22.42, -31.9) * mm, "end": v(-21.48, -30.32) * mm});
            skLineSegment(sketch, "E301", {"start": v(-21.48, -30.32) * mm, "end": v(-21.1, -31.7) * mm});
            skLineSegment(sketch, "E302", {"start": v(-21.1, -31.7) * mm, "end": v(-20.86, -34.03) * mm});
            skLineSegment(sketch, "E303", {"start": v(-20.86, -34.03) * mm, "end": v(-20.15, -34.76) * mm});
            skLineSegment(sketch, "E304", {"start": v(-20.15, -34.76) * mm, "end": v(-20.15, -37.36) * mm});
            skLineSegment(sketch, "E305", {"start": v(-20.15, -37.36) * mm, "end": v(-20, -38.73) * mm});
            skLineSegment(sketch, "E306", {"start": v(-20, -38.73) * mm, "end": v(-18.5, -39.9) * mm});
            skLineSegment(sketch, "E307", {"start": v(-18.5, -39.9) * mm, "end": v(-18.5, -36.32) * mm});
            skLineSegment(sketch, "E308", {"start": v(-18.5, -36.32) * mm, "end": v(-17.03, -36.47) * mm});
            skLineSegment(sketch, "E309", {"start": v(-17.03, -36.47) * mm, "end": v(-18.5, -35.14) * mm});
            skLineSegment(sketch, "E310", {"start": v(-18.5, -35.14) * mm, "end": v(-18.26, -33.07) * mm});
            skLineSegment(sketch, "E311", {"start": v(-18.26, -33.07) * mm, "end": v(-16.97, -33.6) * mm});
            skLineSegment(sketch, "E312", {"start": v(-16.97, -33.6) * mm, "end": v(-18.5, -31.29) * mm});
            skLineSegment(sketch, "E313", {"start": v(-18.5, -31.29) * mm, "end": v(-18.36, -27.93) * mm});
            skLineSegment(sketch, "E314", {"start": v(-18.36, -27.93) * mm, "end": v(-17.5, -26.84) * mm});
            skLineSegment(sketch, "E315", {"start": v(-17.5, -26.84) * mm, "end": v(-17.73, -24.97) * mm});
            skLineSegment(sketch, "E316", {"start": v(-17.73, -24.97) * mm, "end": v(-17.18, -24.19) * mm});
            skLineSegment(sketch, "E317", {"start": v(-17.18, -24.19) * mm, "end": v(-17.68, -22.12) * mm});
            skLineSegment(sketch, "E318", {"start": v(-17.68, -22.12) * mm, "end": v(-16.65, -20.4) * mm});
            skLineSegment(sketch, "E319", {"start": v(-16.65, -20.4) * mm, "end": v(-17.78, -18.32) * mm});
            skLineSegment(sketch, "E320", {"start": v(-17.78, -18.32) * mm, "end": v(-17.78, -14.13) * mm});
            skLineSegment(sketch, "E321", {"start": v(-17.78, -14.13) * mm, "end": v(-17.25, -13.46) * mm});
            skLineSegment(sketch, "E322", {"start": v(-17.25, -13.46) * mm, "end": v(-14.71, -13.71) * mm});
            skLineSegment(sketch, "E323", {"start": v(-14.71, -13.71) * mm, "end": v(-12.69, -12.35) * mm});
            skLineSegment(sketch, "E324", {"start": v(-12.69, -12.35) * mm, "end": v(-10.4, -9.78) * mm});
            skLineSegment(sketch, "E325", {"start": v(-10.4, -9.78) * mm, "end": v(-9.26, -11.38) * mm});
            skLineSegment(sketch, "E326", {"start": v(-9.26, -11.38) * mm, "end": v(-8.14, -7.03) * mm});
            skLineSegment(sketch, "E327", {"start": v(-8.14, -7.03) * mm, "end": v(-8.55, -2.82) * mm});
            skLineSegment(sketch, "E328", {"start": v(-8.55, -2.82) * mm, "end": v(-9.58, 1.57) * mm});
            skLineSegment(sketch, "E329", {"start": v(-9.58, 1.57) * mm, "end": v(-15, 4.5) * mm});
            skLineSegment(sketch, "E330", {"start": v(-15, 4.5) * mm, "end": v(-18.5, 4.5) * mm});
            skLineSegment(sketch, "E331", {"start": v(-18.5, 4.5) * mm, "end": v(-20.04, 3.07) * mm});
            skLineSegment(sketch, "E332", {"start": v(-20.04, 3.07) * mm, "end": v(-21.2, 3.18) * mm});
            skLineSegment(sketch, "E333", {"start": v(-21.2, 3.18) * mm, "end": v(-22.02, 6.06) * mm});
            skLineSegment(sketch, "E334", {"start": v(-15.67, -9.12) * mm, "end": v(-13.15, -7.33) * mm});
            skLineSegment(sketch, "E335", {"start": v(-13.15, -7.33) * mm, "end": v(-12.36, -3.56) * mm});
            skLineSegment(sketch, "E336", {"start": v(-12.36, -3.56) * mm, "end": v(-14.3, 0) * mm});
            skLineSegment(sketch, "E337", {"start": v(-14.3, 0) * mm, "end": v(-17.75, -0.47) * mm});
            skLineSegment(sketch, "E338", {"start": v(-17.75, -0.47) * mm, "end": v(-19.19, -3.73) * mm});
            skLineSegment(sketch, "E339", {"start": v(-19.19, -3.73) * mm, "end": v(-18.85, -7.03) * mm});
            skLineSegment(sketch, "E340", {"start": v(-18.85, -7.03) * mm, "end": v(-17.24, -4.96) * mm});
            skLineSegment(sketch, "E341", {"start": v(-17.24, -4.96) * mm, "end": v(-18.18, -8.6) * mm});
            skLineSegment(sketch, "E342", {"start": v(-18.18, -8.6) * mm, "end": v(-15.67, -9.12) * mm});
            skLineSegment(sketch, "E343", {"start": v(-5.3, 18.28) * mm, "end": v(-6.44, 17.35) * mm});
            skLineSegment(sketch, "E344", {"start": v(-6.44, 17.35) * mm, "end": v(-6.25, 15.5) * mm});
            skLineSegment(sketch, "E345", {"start": v(-6.25, 15.5) * mm, "end": v(-7.18, 14.5) * mm});
            skLineSegment(sketch, "E346", {"start": v(-7.18, 14.5) * mm, "end": v(-7.84, 11.96) * mm});
            skLineSegment(sketch, "E347", {"start": v(-7.84, 11.96) * mm, "end": v(-5.81, 10.04) * mm});
            skLineSegment(sketch, "E348", {"start": v(-5.81, 10.04) * mm, "end": v(-5.81, 4.93) * mm});
            skLineSegment(sketch, "E349", {"start": v(-5.81, 4.93) * mm, "end": v(-7.88, 3) * mm});
            skLineSegment(sketch, "E350", {"start": v(-7.88, 3) * mm, "end": v(-5.44, 0.38) * mm});
            skLineSegment(sketch, "E351", {"start": v(-5.44, 0.38) * mm, "end": v(-7.13, -3.2) * mm});
            skLineSegment(sketch, "E352", {"start": v(-7.13, -3.2) * mm, "end": v(-5.67, -8.12) * mm});
            skLineSegment(sketch, "E353", {"start": v(-5.67, -8.12) * mm, "end": v(-7.99, -12.8) * mm});
            skLineSegment(sketch, "E354", {"start": v(-7.99, -12.8) * mm, "end": v(-7, -14.6) * mm});
            skLineSegment(sketch, "E355", {"start": v(-7, -14.6) * mm, "end": v(-9.63, -17.15) * mm});
            skLineSegment(sketch, "E356", {"start": v(-9.63, -17.15) * mm, "end": v(-7.76, -16.95) * mm});
            skLineSegment(sketch, "E357", {"start": v(-7.76, -16.95) * mm, "end": v(-7.34, -21.05) * mm});
            skLineSegment(sketch, "E358", {"start": v(-7.34, -21.05) * mm, "end": v(-8.66, -21.75) * mm});
            skLineSegment(sketch, "E359", {"start": v(-8.66, -21.75) * mm, "end": v(-8.66, -22.57) * mm});
            skLineSegment(sketch, "E360", {"start": v(-8.66, -22.57) * mm, "end": v(-7.34, -22.53) * mm});
            skLineSegment(sketch, "E361", {"start": v(-7.34, -22.53) * mm, "end": v(-7.99, -25.81) * mm});
            skLineSegment(sketch, "E362", {"start": v(-7.99, -25.81) * mm, "end": v(-6.95, -22.67) * mm});
            skLineSegment(sketch, "E363", {"start": v(-6.95, -22.67) * mm, "end": v(-6.2, -22.92) * mm});
            skLineSegment(sketch, "E364", {"start": v(-6.2, -22.92) * mm, "end": v(-6.2, -26.46) * mm});
            skLineSegment(sketch, "E365", {"start": v(-6.2, -26.46) * mm, "end": v(-7.8, -28.1) * mm});
            skLineSegment(sketch, "E366", {"start": v(-7.8, -28.1) * mm, "end": v(-6.92, -28.63) * mm});
            skLineSegment(sketch, "E367", {"start": v(-6.92, -28.63) * mm, "end": v(-4.85, -34.3) * mm});
            skLineSegment(sketch, "E368", {"start": v(-4.85, -34.3) * mm, "end": v(-2, -27.7) * mm});
            skLineSegment(sketch, "E369", {"start": v(-2, -27.7) * mm, "end": v(-2.42, -26.78) * mm});
            skLineSegment(sketch, "E370", {"start": v(-2.42, -26.78) * mm, "end": v(-2.31, -20.57) * mm});
            skLineSegment(sketch, "E371", {"start": v(-2.31, -20.57) * mm, "end": v(-1.35, -19.57) * mm});
            skLineSegment(sketch, "E372", {"start": v(-1.35, -19.57) * mm, "end": v(-2.28, -18.57) * mm});
            skLineSegment(sketch, "E373", {"start": v(-2.28, -18.57) * mm, "end": v(-2.28, -13.8) * mm});
            skLineSegment(sketch, "E374", {"start": v(-2.28, -13.8) * mm, "end": v(0, -15.97) * mm});
            skLineSegment(sketch, "E375", {"start": v(0, -15.97) * mm, "end": v(0.82, -16.29) * mm});
            skLineSegment(sketch, "E376", {"start": v(0.82, -16.29) * mm, "end": v(0.93, -19.07) * mm});
            skLineSegment(sketch, "E377", {"start": v(0.93, -19.07) * mm, "end": v(1.93, -18.36) * mm});
            skLineSegment(sketch, "E378", {"start": v(1.93, -18.36) * mm, "end": v(3.68, -20.21) * mm});
            skLineSegment(sketch, "E379", {"start": v(3.68, -20.21) * mm, "end": v(4.36, -20.25) * mm});
            skLineSegment(sketch, "E380", {"start": v(4.36, -20.25) * mm, "end": v(4.75, -22.28) * mm});
            skLineSegment(sketch, "E381", {"start": v(4.75, -22.28) * mm, "end": v(3.18, -22.46) * mm});
            skLineSegment(sketch, "E382", {"start": v(3.18, -22.46) * mm, "end": v(5.46, -23.2) * mm});
            skLineSegment(sketch, "E383", {"start": v(5.46, -23.2) * mm, "end": v(6.67, -25.53) * mm});
            skLineSegment(sketch, "E384", {"start": v(6.67, -25.53) * mm, "end": v(9.31, -24.82) * mm});
            skLineSegment(sketch, "E385", {"start": v(9.31, -24.82) * mm, "end": v(11.85, -29.13) * mm});
            skLineSegment(sketch, "E386", {"start": v(11.85, -29.13) * mm, "end": v(13.7, -28.77) * mm});
            skLineSegment(sketch, "E387", {"start": v(13.7, -28.77) * mm, "end": v(15.63, -32.6) * mm});
            skLineSegment(sketch, "E388", {"start": v(15.63, -32.6) * mm, "end": v(16.91, -31.95) * mm});
            skLineSegment(sketch, "E389", {"start": v(16.91, -31.95) * mm, "end": v(19.12, -34.41) * mm});
            skLineSegment(sketch, "E390", {"start": v(19.12, -34.41) * mm, "end": v(18.41, -32.24) * mm});
            skLineSegment(sketch, "E391", {"start": v(18.41, -32.24) * mm, "end": v(18.8, -31.02) * mm});
            skLineSegment(sketch, "E392", {"start": v(18.8, -31.02) * mm, "end": v(16.88, -28.7) * mm});
            skLineSegment(sketch, "E393", {"start": v(16.88, -28.7) * mm, "end": v(13.02, -24.89) * mm});
            skLineSegment(sketch, "E394", {"start": v(13.02, -24.89) * mm, "end": v(7.39, -18.6) * mm});
            skLineSegment(sketch, "E395", {"start": v(7.39, -18.6) * mm, "end": v(3.18, -13.38) * mm});
            skLineSegment(sketch, "E396", {"start": v(3.18, -13.38) * mm, "end": v(1.47, -11.04) * mm});
            skLineSegment(sketch, "E397", {"start": v(1.47, -11.04) * mm, "end": v(1.05, -9) * mm});
            skLineSegment(sketch, "E398", {"start": v(1.05, -9) * mm, "end": v(6.13, -4.45) * mm});
            skLineSegment(sketch, "E399", {"start": v(6.13, -4.45) * mm, "end": v(6.19, -2.23) * mm});
            skLineSegment(sketch, "E400", {"start": v(6.19, -2.23) * mm, "end": v(11.7, 2.93) * mm});
            skLineSegment(sketch, "E401", {"start": v(11.7, 2.93) * mm, "end": v(15.49, 6.77) * mm});
            skLineSegment(sketch, "E402", {"start": v(15.49, 6.77) * mm, "end": v(13.99, 7.43) * mm});
            skLineSegment(sketch, "E403", {"start": v(13.99, 7.43) * mm, "end": v(16.09, 10.07) * mm});
            skLineSegment(sketch, "E404", {"start": v(16.09, 10.07) * mm, "end": v(8, 3.57) * mm});
            skLineSegment(sketch, "E405", {"start": v(8, 3.57) * mm, "end": v(6.8, 3.5) * mm});
            skLineSegment(sketch, "E406", {"start": v(6.8, 3.5) * mm, "end": v(7.64, 2.97) * mm});
            skLineSegment(sketch, "E407", {"start": v(7.64, 2.97) * mm, "end": v(5.96, 1.89) * mm});
            skLineSegment(sketch, "E408", {"start": v(5.96, 1.89) * mm, "end": v(5.6, 2.34) * mm});
            skLineSegment(sketch, "E409", {"start": v(5.6, 2.34) * mm, "end": v(3.7, 1.29) * mm});
            skLineSegment(sketch, "E410", {"start": v(3.7, 1.29) * mm, "end": v(3.32, -0.57) * mm});
            skLineSegment(sketch, "E411", {"start": v(3.32, -0.57) * mm, "end": v(2.39, -1.14) * mm});
            skLineSegment(sketch, "E412", {"start": v(2.39, -1.14) * mm, "end": v(2.75, -1.71) * mm});
            skLineSegment(sketch, "E413", {"start": v(2.75, -1.71) * mm, "end": v(1.97, -2.4) * mm});
            skLineSegment(sketch, "E414", {"start": v(1.97, -2.4) * mm, "end": v(1.16, -0.9) * mm});
            skLineSegment(sketch, "E415", {"start": v(1.16, -0.9) * mm, "end": v(-0.82, -2.58) * mm});
            skLineSegment(sketch, "E416", {"start": v(-0.82, -2.58) * mm, "end": v(-1.2, -3.7) * mm});
            skLineSegment(sketch, "E417", {"start": v(-1.2, -3.7) * mm, "end": v(-1.93, -3.84) * mm});
            skLineSegment(sketch, "E418", {"start": v(-1.93, -3.84) * mm, "end": v(-2.05, -2.22) * mm});
            skLineSegment(sketch, "E419", {"start": v(-2.05, -2.22) * mm, "end": v(-1.72, 0.6) * mm});
            skLineSegment(sketch, "E420", {"start": v(-1.72, 0.6) * mm, "end": v(-2.56, 1.23) * mm});
            skLineSegment(sketch, "E421", {"start": v(-2.56, 1.23) * mm, "end": v(-2.02, 2.28) * mm});
            skLineSegment(sketch, "E422", {"start": v(-2.02, 2.28) * mm, "end": v(-2.32, 3.36) * mm});
            skLineSegment(sketch, "E423", {"start": v(-2.32, 3.36) * mm, "end": v(-1.48, 3.87) * mm});
            skLineSegment(sketch, "E424", {"start": v(-1.48, 3.87) * mm, "end": v(-1.57, 4.62) * mm});
            skLineSegment(sketch, "E425", {"start": v(-1.57, 4.62) * mm, "end": v(-2.11, 4.7) * mm});
            skLineSegment(sketch, "E426", {"start": v(-2.11, 4.7) * mm, "end": v(-1.78, 6.48) * mm});
            skLineSegment(sketch, "E427", {"start": v(-1.78, 6.48) * mm, "end": v(-1.21, 7.38) * mm});
            skLineSegment(sketch, "E428", {"start": v(-1.21, 7.38) * mm, "end": v(-0.85, 8.34) * mm});
            skLineSegment(sketch, "E429", {"start": v(-0.85, 8.34) * mm, "end": v(-1.27, 9.03) * mm});
            skLineSegment(sketch, "E430", {"start": v(-1.27, 9.03) * mm, "end": v(-1.12, 11.49) * mm});
            skLineSegment(sketch, "E431", {"start": v(-1.12, 11.49) * mm, "end": v(-0.79, 14.6) * mm});
            skLineSegment(sketch, "E432", {"start": v(-0.79, 14.6) * mm, "end": v(-1.57, 15.01) * mm});
            skLineSegment(sketch, "E433", {"start": v(-1.57, 15.01) * mm, "end": v(-0.66, 15.87) * mm});
            skLineSegment(sketch, "E434", {"start": v(-0.66, 15.87) * mm, "end": v(-1.77, 16.47) * mm});
            skLineSegment(sketch, "E435", {"start": v(-1.77, 16.47) * mm, "end": v(-2.65, 18.16) * mm});
            skLineSegment(sketch, "E436", {"start": v(-2.65, 18.16) * mm, "end": v(-4.52, 17.79) * mm});
            skLineSegment(sketch, "E437", {"start": v(-4.52, 17.79) * mm, "end": v(-5.3, 18.28) * mm});
            skLineSegment(sketch, "E438", {"start": v(16.26, -23) * mm, "end": v(15, -23) * mm});
            skLineSegment(sketch, "E439", {"start": v(15, -23) * mm, "end": v(15.66, -23.68) * mm});
            skLineSegment(sketch, "E440", {"start": v(15.66, -23.68) * mm, "end": v(14.76, -23.9) * mm});
            skLineSegment(sketch, "E441", {"start": v(14.76, -23.9) * mm, "end": v(13.74, -22.75) * mm});
            skLineSegment(sketch, "E442", {"start": v(13.74, -22.75) * mm, "end": v(12.6, -23.34) * mm});
            skLineSegment(sketch, "E443", {"start": v(12.6, -23.34) * mm, "end": v(11.46, -21.05) * mm});
            skLineSegment(sketch, "E444", {"start": v(11.46, -21.05) * mm, "end": v(9.5, -19.16) * mm});
            skLineSegment(sketch, "E445", {"start": v(9.5, -19.16) * mm, "end": v(7.7, -15.7) * mm});
            skLineSegment(sketch, "E446", {"start": v(7.7, -15.7) * mm, "end": v(8.79, -15.17) * mm});
            skLineSegment(sketch, "E447", {"start": v(8.79, -15.17) * mm, "end": v(8.76, -13.58) * mm});
            skLineSegment(sketch, "E448", {"start": v(8.76, -13.58) * mm, "end": v(7.02, -12.56) * mm});
            skLineSegment(sketch, "E449", {"start": v(7.02, -12.56) * mm, "end": v(9.42, -12.95) * mm});
            skLineSegment(sketch, "E450", {"start": v(9.42, -12.95) * mm, "end": v(8.39, -10.97) * mm});
            skLineSegment(sketch, "E451", {"start": v(8.39, -10.97) * mm, "end": v(10, -9.03) * mm});
            skLineSegment(sketch, "E452", {"start": v(10, -9.03) * mm, "end": v(8.5, -5.96) * mm});
            skLineSegment(sketch, "E453", {"start": v(8.5, -5.96) * mm, "end": v(9.35, -1.71) * mm});
            skLineSegment(sketch, "E454", {"start": v(9.35, -1.71) * mm, "end": v(12.22, -0.21) * mm});
            skLineSegment(sketch, "E455", {"start": v(12.22, -0.21) * mm, "end": v(12.92, 2) * mm});
            skLineSegment(sketch, "E456", {"start": v(12.92, 2) * mm, "end": v(14.41, 0.78) * mm});
            skLineSegment(sketch, "E457", {"start": v(14.41, 0.78) * mm, "end": v(14.41, -2.5) * mm});
            skLineSegment(sketch, "E458", {"start": v(14.41, -2.5) * mm, "end": v(13.63, -3.29) * mm});
            skLineSegment(sketch, "E459", {"start": v(13.63, -3.29) * mm, "end": v(14.27, -4.82) * mm});
            skLineSegment(sketch, "E460", {"start": v(14.27, -4.82) * mm, "end": v(17.59, -1.47) * mm});
            skLineSegment(sketch, "E461", {"start": v(17.59, -1.47) * mm, "end": v(18.3, -0.11) * mm});
            skLineSegment(sketch, "E462", {"start": v(18.3, -0.11) * mm, "end": v(20.26, -0.4) * mm});
            skLineSegment(sketch, "E463", {"start": v(20.26, -0.4) * mm, "end": v(21.87, 1.5) * mm});
            skLineSegment(sketch, "E464", {"start": v(21.87, 1.5) * mm, "end": v(23.37, 2.56) * mm});
            skLineSegment(sketch, "E465", {"start": v(23.37, 2.56) * mm, "end": v(24.65, 1.17) * mm});
            skLineSegment(sketch, "E466", {"start": v(24.65, 1.17) * mm, "end": v(24.69, -0.65) * mm});
            skLineSegment(sketch, "E467", {"start": v(24.69, -0.65) * mm, "end": v(26.33, -0.11) * mm});
            skLineSegment(sketch, "E468", {"start": v(26.33, -0.11) * mm, "end": v(26.44, -1.75) * mm});
            skLineSegment(sketch, "E469", {"start": v(26.44, -1.75) * mm, "end": v(28.64, -5.97) * mm});
            skLineSegment(sketch, "E470", {"start": v(28.64, -5.97) * mm, "end": v(29.58, -9.53) * mm});
            skLineSegment(sketch, "E471", {"start": v(29.58, -9.53) * mm, "end": v(29.86, -13.1) * mm});
            skLineSegment(sketch, "E472", {"start": v(29.86, -13.1) * mm, "end": v(30.9, -13.42) * mm});
            skLineSegment(sketch, "E473", {"start": v(30.9, -13.42) * mm, "end": v(29.18, -14.13) * mm});
            skLineSegment(sketch, "E474", {"start": v(29.18, -14.13) * mm, "end": v(29.68, -17.06) * mm});
            skLineSegment(sketch, "E475", {"start": v(29.68, -17.06) * mm, "end": v(28.43, -19.27) * mm});
            skLineSegment(sketch, "E476", {"start": v(28.43, -19.27) * mm, "end": v(29.99, -19.78) * mm});
            skLineSegment(sketch, "E477", {"start": v(29.99, -19.78) * mm, "end": v(28.33, -21.8) * mm});
            skLineSegment(sketch, "E478", {"start": v(28.33, -21.8) * mm, "end": v(29.97, -24.23) * mm});
            skLineSegment(sketch, "E479", {"start": v(29.97, -24.23) * mm, "end": v(29.04, -26.26) * mm});
            skLineSegment(sketch, "E480", {"start": v(29.04, -26.26) * mm, "end": v(28.26, -27.3) * mm});
            skLineSegment(sketch, "E481", {"start": v(28.26, -27.3) * mm, "end": v(27.5, -31.22) * mm});
            skLineSegment(sketch, "E482", {"start": v(27.5, -31.22) * mm, "end": v(25.97, -28.68) * mm});
            skLineSegment(sketch, "E483", {"start": v(25.97, -28.68) * mm, "end": v(24.9, -28.65) * mm});
            skLineSegment(sketch, "E484", {"start": v(24.9, -28.65) * mm, "end": v(25.4, -27.5) * mm});
            skLineSegment(sketch, "E485", {"start": v(25.4, -27.5) * mm, "end": v(24.12, -26.26) * mm});
            skLineSegment(sketch, "E486", {"start": v(24.12, -26.26) * mm, "end": v(23.08, -22.66) * mm});
            skLineSegment(sketch, "E487", {"start": v(23.08, -22.66) * mm, "end": v(24.37, -19.48) * mm});
            skLineSegment(sketch, "E488", {"start": v(24.37, -19.48) * mm, "end": v(23.23, -17.91) * mm});
            skLineSegment(sketch, "E489", {"start": v(23.23, -17.91) * mm, "end": v(24.44, -14.45) * mm});
            skLineSegment(sketch, "E490", {"start": v(24.44, -14.45) * mm, "end": v(23.4, -12.49) * mm});
            skLineSegment(sketch, "E491", {"start": v(23.4, -12.49) * mm, "end": v(24.65, -10.53) * mm});
            skLineSegment(sketch, "E492", {"start": v(24.65, -10.53) * mm, "end": v(21.4, -6) * mm});
            skLineSegment(sketch, "E493", {"start": v(21.4, -6) * mm, "end": v(21.62, -4.03) * mm});
            skLineSegment(sketch, "E494", {"start": v(21.62, -4.03) * mm, "end": v(18.9, -5.89) * mm});
            skLineSegment(sketch, "E495", {"start": v(18.9, -5.89) * mm, "end": v(16.3, -6.71) * mm});
            skLineSegment(sketch, "E496", {"start": v(16.3, -6.71) * mm, "end": v(15.63, -11.7) * mm});
            skLineSegment(sketch, "E497", {"start": v(15.63, -11.7) * mm, "end": v(15.48, -16.02) * mm});
            skLineSegment(sketch, "E498", {"start": v(15.48, -16.02) * mm, "end": v(15.91, -17.34) * mm});
            skLineSegment(sketch, "E499", {"start": v(15.91, -17.34) * mm, "end": v(14.34, -18.87) * mm});
            skLineSegment(sketch, "E500", {"start": v(14.34, -18.87) * mm, "end": v(16.26, -23) * mm});
            skLineSegment(sketch, "E501", {"start": v(31.33, -1.71) * mm, "end": v(29.72, -1.71) * mm});
            skLineSegment(sketch, "E502", {"start": v(29.72, -1.71) * mm, "end": v(28.83, -3.7) * mm});
            skLineSegment(sketch, "E503", {"start": v(28.83, -3.7) * mm, "end": v(30.31, -4.76) * mm});
            skLineSegment(sketch, "E504", {"start": v(30.31, -4.76) * mm, "end": v(31.16, -10.02) * mm});
            skLineSegment(sketch, "E505", {"start": v(31.16, -10.02) * mm, "end": v(31.57, -13.28) * mm});
            skLineSegment(sketch, "E506", {"start": v(31.57, -13.28) * mm, "end": v(34.2, -16.76) * mm});
            skLineSegment(sketch, "E507", {"start": v(34.2, -16.76) * mm, "end": v(32.53, -18.62) * mm});
            skLineSegment(sketch, "E508", {"start": v(32.53, -18.62) * mm, "end": v(36.67, -23.48) * mm});
            skLineSegment(sketch, "E509", {"start": v(36.67, -23.48) * mm, "end": v(40.87, -25.82) * mm});
            skLineSegment(sketch, "E510", {"start": v(40.87, -25.82) * mm, "end": v(43.57, -23.3) * mm});
            skLineSegment(sketch, "E511", {"start": v(43.57, -23.3) * mm, "end": v(45.37, -20.96) * mm});
            skLineSegment(sketch, "E512", {"start": v(45.37, -20.96) * mm, "end": v(48.97, -15.08) * mm});
            skLineSegment(sketch, "E513", {"start": v(48.97, -15.08) * mm, "end": v(48.68, -12.1) * mm});
            skLineSegment(sketch, "E514", {"start": v(48.68, -12.1) * mm, "end": v(49.48, -11.44) * mm});
            skLineSegment(sketch, "E515", {"start": v(49.48, -11.44) * mm, "end": v(47.97, -9.57) * mm});
            skLineSegment(sketch, "E516", {"start": v(47.97, -9.57) * mm, "end": v(48.6, -6.52) * mm});
            skLineSegment(sketch, "E517", {"start": v(48.6, -6.52) * mm, "end": v(47.63, -5.56) * mm});
            skLineSegment(sketch, "E518", {"start": v(47.63, -5.56) * mm, "end": v(48.65, -2.44) * mm});
            skLineSegment(sketch, "E519", {"start": v(48.65, -2.44) * mm, "end": v(45.41, 2.18) * mm});
            skLineSegment(sketch, "E520", {"start": v(45.41, 2.18) * mm, "end": v(39.95, 6.02) * mm});
            skLineSegment(sketch, "E521", {"start": v(39.95, 6.02) * mm, "end": v(38.46, 6.27) * mm});
            skLineSegment(sketch, "E522", {"start": v(38.46, 6.27) * mm, "end": v(38.36, 7.2) * mm});
            skLineSegment(sketch, "E523", {"start": v(38.36, 7.2) * mm, "end": v(41.6, 7.55) * mm});
            skLineSegment(sketch, "E524", {"start": v(41.6, 7.55) * mm, "end": v(42.2, 6.12) * mm});
            skLineSegment(sketch, "E525", {"start": v(42.2, 6.12) * mm, "end": v(43.66, 7.33) * mm});
            skLineSegment(sketch, "E526", {"start": v(43.66, 7.33) * mm, "end": v(46.33, 6.95) * mm});
            skLineSegment(sketch, "E527", {"start": v(46.33, 6.95) * mm, "end": v(46.33, 5.14) * mm});
            skLineSegment(sketch, "E528", {"start": v(46.33, 5.14) * mm, "end": v(48.68, 6.5) * mm});
            skLineSegment(sketch, "E529", {"start": v(48.68, 6.5) * mm, "end": v(49.84, 7.76) * mm});
            skLineSegment(sketch, "E530", {"start": v(49.84, 7.76) * mm, "end": v(51.58, 5.19) * mm});
            skLineSegment(sketch, "E531", {"start": v(51.58, 5.19) * mm, "end": v(48.89, 3.36) * mm});
            skLineSegment(sketch, "E532", {"start": v(48.89, 3.36) * mm, "end": v(50.88, 0.04) * mm});
            skLineSegment(sketch, "E533", {"start": v(50.88, 0.04) * mm, "end": v(50.04, -2.6) * mm});
            skLineSegment(sketch, "E534", {"start": v(50.04, -2.6) * mm, "end": v(51.36, -4.16) * mm});
            skLineSegment(sketch, "E535", {"start": v(51.36, -4.16) * mm, "end": v(51.36, -13.32) * mm});
            skLineSegment(sketch, "E536", {"start": v(51.36, -13.32) * mm, "end": v(52.7, -11.28) * mm});
            skLineSegment(sketch, "E537", {"start": v(52.7, -11.28) * mm, "end": v(52.92, -20.06) * mm});
            skLineSegment(sketch, "E538", {"start": v(52.92, -20.06) * mm, "end": v(51.32, -25) * mm});
            skLineSegment(sketch, "E539", {"start": v(51.32, -25) * mm, "end": v(52.68, -28.71) * mm});
            skLineSegment(sketch, "E540", {"start": v(52.68, -28.71) * mm, "end": v(52.32, -31.42) * mm});
            skLineSegment(sketch, "E541", {"start": v(52.32, -31.42) * mm, "end": v(54.32, -34.35) * mm});
            skLineSegment(sketch, "E542", {"start": v(54.32, -34.35) * mm, "end": v(55.6, -33.63) * mm});
            skLineSegment(sketch, "E543", {"start": v(55.6, -33.63) * mm, "end": v(56.89, -38.98) * mm});
            skLineSegment(sketch, "E544", {"start": v(56.89, -38.98) * mm, "end": v(57.75, -33.85) * mm});
            skLineSegment(sketch, "E545", {"start": v(57.75, -33.85) * mm, "end": v(57.39, -30.85) * mm});
            skLineSegment(sketch, "E546", {"start": v(57.39, -30.85) * mm, "end": v(57.32, -23.07) * mm});
            skLineSegment(sketch, "E547", {"start": v(57.32, -23.07) * mm, "end": v(56.25, -18.08) * mm});
            skLineSegment(sketch, "E548", {"start": v(56.25, -18.08) * mm, "end": v(58.17, -14.94) * mm});
            skLineSegment(sketch, "E549", {"start": v(58.17, -14.94) * mm, "end": v(59.03, -14.66) * mm});
            skLineSegment(sketch, "E550", {"start": v(59.03, -14.66) * mm, "end": v(58.89, -11.52) * mm});
            skLineSegment(sketch, "E551", {"start": v(58.89, -11.52) * mm, "end": v(56.53, -10.02) * mm});
            skLineSegment(sketch, "E552", {"start": v(56.53, -10.02) * mm, "end": v(56.32, -7.02) * mm});
            skLineSegment(sketch, "E553", {"start": v(56.32, -7.02) * mm, "end": v(57.82, -6.24) * mm});
            skLineSegment(sketch, "E554", {"start": v(57.82, -6.24) * mm, "end": v(56.25, -5.1) * mm});
            skLineSegment(sketch, "E555", {"start": v(56.25, -5.1) * mm, "end": v(56.32, -0.46) * mm});
            skLineSegment(sketch, "E556", {"start": v(56.32, -0.46) * mm, "end": v(58.1, -1.81) * mm});
            skLineSegment(sketch, "E557", {"start": v(58.1, -1.81) * mm, "end": v(56.53, 0.9) * mm});
            skLineSegment(sketch, "E558", {"start": v(56.53, 0.9) * mm, "end": v(56.82, 4.54) * mm});
            skLineSegment(sketch, "E559", {"start": v(56.82, 4.54) * mm, "end": v(56.64, 6.18) * mm});
            skLineSegment(sketch, "E560", {"start": v(56.64, 6.18) * mm, "end": v(59.28, 6.72) * mm});
            skLineSegment(sketch, "E561", {"start": v(59.28, 6.72) * mm, "end": v(61.31, 5.11) * mm});
            skLineSegment(sketch, "E562", {"start": v(61.31, 5.11) * mm, "end": v(64.7, 6.92) * mm});
            skLineSegment(sketch, "E563", {"start": v(64.7, 6.92) * mm, "end": v(65.65, 5.9) * mm});
            skLineSegment(sketch, "E564", {"start": v(65.65, 5.9) * mm, "end": v(68.43, 7.17) * mm});
            skLineSegment(sketch, "E565", {"start": v(68.43, 7.17) * mm, "end": v(70.7, 5.2) * mm});
            skLineSegment(sketch, "E566", {"start": v(70.7, 5.2) * mm, "end": v(72.36, 7.07) * mm});
            skLineSegment(sketch, "E567", {"start": v(72.36, 7.07) * mm, "end": v(74.73, 7.27) * mm});
            skLineSegment(sketch, "E568", {"start": v(74.73, 7.27) * mm, "end": v(75.29, 8.58) * mm});
            skLineSegment(sketch, "E569", {"start": v(75.29, 8.58) * mm, "end": v(75.74, 10.04) * mm});
            skLineSegment(sketch, "E570", {"start": v(75.74, 10.04) * mm, "end": v(65.96, 9.84) * mm});
            skLineSegment(sketch, "E571", {"start": v(65.96, 9.84) * mm, "end": v(66.1, 10.8) * mm});
            skLineSegment(sketch, "E572", {"start": v(66.1, 10.8) * mm, "end": v(64.7, 9.8) * mm});
            skLineSegment(sketch, "E573", {"start": v(64.7, 9.8) * mm, "end": v(58.7, 10.1) * mm});
            skLineSegment(sketch, "E574", {"start": v(58.7, 10.1) * mm, "end": v(56.87, 10.65) * mm});
            skLineSegment(sketch, "E575", {"start": v(56.87, 10.65) * mm, "end": v(55.87, 11.2) * mm});
            skLineSegment(sketch, "E576", {"start": v(55.87, 11.2) * mm, "end": v(53.9, 10.95) * mm});
            skLineSegment(sketch, "E577", {"start": v(53.9, 10.95) * mm, "end": v(53.7, 9.9) * mm});
            skLineSegment(sketch, "E578", {"start": v(53.7, 9.9) * mm, "end": v(52.08, 9.74) * mm});
            skLineSegment(sketch, "E579", {"start": v(52.08, 9.74) * mm, "end": v(51.07, 11.05) * mm});
            skLineSegment(sketch, "E580", {"start": v(51.07, 11.05) * mm, "end": v(49.4, 10.14) * mm});
            skLineSegment(sketch, "E581", {"start": v(49.4, 10.14) * mm, "end": v(47.95, 10.55) * mm});
            skLineSegment(sketch, "E582", {"start": v(47.95, 10.55) * mm, "end": v(45.22, 10.7) * mm});
            skLineSegment(sketch, "E583", {"start": v(45.22, 10.7) * mm, "end": v(43.6, 11.96) * mm});
            skLineSegment(sketch, "E584", {"start": v(43.6, 11.96) * mm, "end": v(43.86, 10.55) * mm});
            skLineSegment(sketch, "E585", {"start": v(43.86, 10.55) * mm, "end": v(42.8, 10.3) * mm});
            skLineSegment(sketch, "E586", {"start": v(42.8, 10.3) * mm, "end": v(42.3, 11.76) * mm});
            skLineSegment(sketch, "E587", {"start": v(42.3, 11.76) * mm, "end": v(41.49, 10.4) * mm});
            skLineSegment(sketch, "E588", {"start": v(41.49, 10.4) * mm, "end": v(39.82, 10.65) * mm});
            skLineSegment(sketch, "E589", {"start": v(39.82, 10.65) * mm, "end": v(39.32, 11.4) * mm});
            skLineSegment(sketch, "E590", {"start": v(39.32, 11.4) * mm, "end": v(38.3, 10.95) * mm});
            skLineSegment(sketch, "E591", {"start": v(38.3, 10.95) * mm, "end": v(36.95, 10.65) * mm});
            skLineSegment(sketch, "E592", {"start": v(36.95, 10.65) * mm, "end": v(36.6, 12.21) * mm});
            skLineSegment(sketch, "E593", {"start": v(36.6, 12.21) * mm, "end": v(35.28, 10.95) * mm});
            skLineSegment(sketch, "E594", {"start": v(35.28, 10.95) * mm, "end": v(33.72, 11.46) * mm});
            skLineSegment(sketch, "E595", {"start": v(33.72, 11.46) * mm, "end": v(32.6, 10.14) * mm});
            skLineSegment(sketch, "E596", {"start": v(32.6, 10.14) * mm, "end": v(33.26, 9.49) * mm});
            skLineSegment(sketch, "E597", {"start": v(33.26, 9.49) * mm, "end": v(31.35, 9.08) * mm});
            skLineSegment(sketch, "E598", {"start": v(31.35, 9.08) * mm, "end": v(30.8, 8.83) * mm});
            skLineSegment(sketch, "E599", {"start": v(30.8, 8.83) * mm, "end": v(31.9, 7.42) * mm});
            skLineSegment(sketch, "E600", {"start": v(31.9, 7.42) * mm, "end": v(33.37, 7.07) * mm});
            skLineSegment(sketch, "E601", {"start": v(33.37, 7.07) * mm, "end": v(35.33, 7.27) * mm});
            skLineSegment(sketch, "E602", {"start": v(35.33, 7.27) * mm, "end": v(36.75, 6.61) * mm});
            skLineSegment(sketch, "E603", {"start": v(36.75, 6.61) * mm, "end": v(35.64, 5.9) * mm});
            skLineSegment(sketch, "E604", {"start": v(35.64, 5.9) * mm, "end": v(35.18, 5.1) * mm});
            skLineSegment(sketch, "E605", {"start": v(35.18, 5.1) * mm, "end": v(34.53, 5.6) * mm});
            skLineSegment(sketch, "E606", {"start": v(34.53, 5.6) * mm, "end": v(31.9, 2.78) * mm});
            skLineSegment(sketch, "E607", {"start": v(31.9, 2.78) * mm, "end": v(31.9, 1.26) * mm});
            skLineSegment(sketch, "E608", {"start": v(31.9, 1.26) * mm, "end": v(29.99, 0.2) * mm});
            skLineSegment(sketch, "E609", {"start": v(29.99, 0.2) * mm, "end": v(31.65, -0.3) * mm});
            skLineSegment(sketch, "E610", {"start": v(31.65, -0.3) * mm, "end": v(31.33, -1.71) * mm});
            skLineSegment(sketch, "E611", {"start": v(35.97, -7.7) * mm, "end": v(36.99, -4.76) * mm});
            skLineSegment(sketch, "E612", {"start": v(36.99, -4.76) * mm, "end": v(38.94, -3.37) * mm});
            skLineSegment(sketch, "E613", {"start": v(38.94, -3.37) * mm, "end": v(36.7, -2.77) * mm});
            skLineSegment(sketch, "E614", {"start": v(36.7, -2.77) * mm, "end": v(37.37, -1.92) * mm});
            skLineSegment(sketch, "E615", {"start": v(37.37, -1.92) * mm, "end": v(37.71, -2.48) * mm});
            skLineSegment(sketch, "E616", {"start": v(37.71, -2.48) * mm, "end": v(38, -0.6) * mm});
            skLineSegment(sketch, "E617", {"start": v(38, -0.6) * mm, "end": v(39.07, -0.14) * mm});
            skLineSegment(sketch, "E618", {"start": v(39.07, -0.14) * mm, "end": v(39.75, -0.52) * mm});
            skLineSegment(sketch, "E619", {"start": v(39.75, -0.52) * mm, "end": v(40.85, 0.92) * mm});
            skLineSegment(sketch, "E620", {"start": v(40.85, 0.92) * mm, "end": v(42.25, 0.7) * mm});
            skLineSegment(sketch, "E621", {"start": v(42.25, 0.7) * mm, "end": v(42.67, -2.14) * mm});
            skLineSegment(sketch, "E622", {"start": v(42.67, -2.14) * mm, "end": v(42.3, -2.86) * mm});
            skLineSegment(sketch, "E623", {"start": v(42.3, -2.86) * mm, "end": v(43.57, -2.4) * mm});
            skLineSegment(sketch, "E624", {"start": v(43.57, -2.4) * mm, "end": v(43.48, -4.85) * mm});
            skLineSegment(sketch, "E625", {"start": v(43.48, -4.85) * mm, "end": v(42.84, -5.06) * mm});
            skLineSegment(sketch, "E626", {"start": v(42.84, -5.06) * mm, "end": v(44.16, -5.83) * mm});
            skLineSegment(sketch, "E627", {"start": v(44.16, -5.83) * mm, "end": v(44.24, -11.68) * mm});
            skLineSegment(sketch, "E628", {"start": v(44.24, -11.68) * mm, "end": v(44.75, -12.06) * mm});
            skLineSegment(sketch, "E629", {"start": v(44.75, -12.06) * mm, "end": v(44.07, -12.57) * mm});
            skLineSegment(sketch, "E630", {"start": v(44.07, -12.57) * mm, "end": v(43.6, -14.48) * mm});
            skLineSegment(sketch, "E631", {"start": v(43.6, -14.48) * mm, "end": v(44.18, -15.06) * mm});
            skLineSegment(sketch, "E632", {"start": v(44.18, -15.06) * mm, "end": v(42.82, -16.55) * mm});
            skLineSegment(sketch, "E633", {"start": v(42.82, -16.55) * mm, "end": v(42.04, -15.88) * mm});
            skLineSegment(sketch, "E634", {"start": v(42.04, -15.88) * mm, "end": v(41.07, -18.16) * mm});
            skLineSegment(sketch, "E635", {"start": v(41.07, -18.16) * mm, "end": v(39.22, -17.59) * mm});
            skLineSegment(sketch, "E636", {"start": v(39.22, -17.59) * mm, "end": v(40.33, -16.02) * mm});
            skLineSegment(sketch, "E637", {"start": v(40.33, -16.02) * mm, "end": v(37.76, -16.73) * mm});
            skLineSegment(sketch, "E638", {"start": v(37.76, -16.73) * mm, "end": v(37, -14.95) * mm});
            skLineSegment(sketch, "E639", {"start": v(37, -14.95) * mm, "end": v(35.83, -14.02) * mm});
            skLineSegment(sketch, "E640", {"start": v(35.83, -14.02) * mm, "end": v(35.97, -7.7) * mm});
            skFitSpline(sketch, "E641", {"points": [v(-1.36, 67.1) * mm, v(-0.18, 53.22) * mm, v(-1.6, 45.58) * mm, v(-3.77, 43.86) * mm, v(-5.47, 41.32) * mm, v(-6.14, 40.86) * mm, v(-6.78, 40.88) * mm, v(-6.8, 41.52) * mm], "startDerivative": vector(6.04, -47.62) * mm, "endDerivative": vector(2.23, 12.22) * mm});
            skLineSegment(sketch, "E642", {"start": v(-6.78, 41.52) * mm, "end": v(-8.13, 45.66) * mm});
            skLineSegment(sketch, "E643", {"start": v(-8.13, 45.66) * mm, "end": v(-8.16, 40.26) * mm});
            skLineSegment(sketch, "E644", {"start": v(-8.16, 40.26) * mm, "end": v(-7.78, 36.23) * mm});
            skFitSpline(sketch, "E645", {"points": [v(-7.78, 36.23) * mm, v(-9.2, 30.17) * mm, v(-9.37, 23.49) * mm, v(-8.74, 20) * mm, v(-7.52, 15.86) * mm], "startDerivative": vector(-6.08, -21.02) * mm, "endDerivative": vector(5.78, -18.82) * mm});
            skLineSegment(sketch, "E646", {"start": v(-7.52, 15.86) * mm, "end": v(-7.28, 16.01) * mm});
            skLineSegment(sketch, "E647", {"start": v(-7.28, 16.01) * mm, "end": v(-7.34, 17.82) * mm});
            skLineSegment(sketch, "E648", {"start": v(-7.34, 17.82) * mm, "end": v(-5.9, 19.31) * mm});
            skLineSegment(sketch, "E649", {"start": v(-5.9, 19.31) * mm, "end": v(-5.18, 19.37) * mm});
            skLineSegment(sketch, "E650", {"start": v(-5.18, 19.37) * mm, "end": v(-4.32, 18.71) * mm});
            skLineSegment(sketch, "E651", {"start": v(-4.32, 18.71) * mm, "end": v(-4.9, 19.78) * mm});
            skLineSegment(sketch, "E652", {"start": v(-4.9, 19.78) * mm, "end": v(-5.53, 22.25) * mm});
            skFitSpline(sketch, "E653", {"points": [v(-5.53, 22.25) * mm, v(-5.79, 27.1) * mm, v(-4.67, 33.25) * mm, v(-1.95, 37.47) * mm, v(1.06, 32.55) * mm], "startDerivative": vector(-1.94, 20.22) * mm, "endDerivative": vector(11.43, -28.85) * mm});
            skLineSegment(sketch, "E654", {"start": v(1.06, 32.55) * mm, "end": v(0.48, 38.9) * mm});
            skFitSpline(sketch, "E655", {"points": [v(0.48, 38.9) * mm, v(2.15, 38.9) * mm, v(4.96, 37.67) * mm, v(7.18, 34.34) * mm, v(8.7, 26.9) * mm, v(6.42, 20.54) * mm, v(4.11, 19.52) * mm, v(1.18, 20.02) * mm, v(-0.66, 22.89) * mm, v(-0.93, 26.75) * mm], "startDerivative": vector(20.95, 2.07) * mm, "endDerivative": vector(0.83, 34.93) * mm});
            skFitSpline(sketch, "E656", {"points": [v(-0.93, 26.75) * mm, v(-2.26, 22.81) * mm, v(-2.13, 19.48) * mm, v(0, 16.5) * mm, v(4.55, 12.59) * mm, v(9.72, 6.09) * mm], "startDerivative": vector(-8.8, -21.6) * mm, "endDerivative": vector(19.24, -27.09) * mm});
            skLineSegment(sketch, "E657", {"start": v(9.72, 6.09) * mm, "end": v(12.43, 8.7) * mm});
            skFitSpline(sketch, "E658", {"points": [v(12.43, 8.7) * mm, v(11.52, 11.16) * mm, v(10.4, 13.85) * mm, v(9.93, 16.55) * mm, v(9.83, 17.7) * mm, v(9.96, 18.07) * mm, v(10.14, 18.2) * mm, v(10.46, 18.23) * mm, v(10.75, 18) * mm, v(10.93, 17.6) * mm, v(12.64, 15.79) * mm, v(14.25, 14.52) * mm, v(15.14, 13.98) * mm], "startDerivative": vector(-6.77, 19.74) * mm, "endDerivative": vector(10.78, -6.22) * mm});
            skLineSegment(sketch, "E659", {"start": v(15.14, 13.98) * mm, "end": v(15.97, 13.98) * mm});
            skLineSegment(sketch, "E660", {"start": v(15.97, 13.98) * mm, "end": v(14.63, 15.38) * mm});
            skFitSpline(sketch, "E661", {"points": [v(14.63, 15.38) * mm, v(12.28, 18.98) * mm, v(10.85, 22.83) * mm, v(11.34, 25.18) * mm, v(12.08, 30.53) * mm, v(11.26, 34.78) * mm, v(12.16, 36.5) * mm, v(13.04, 40.6) * mm, v(13.1, 44.75) * mm], "startDerivative": vector(-18.22, 25.57) * mm, "endDerivative": vector(-0.53, 30.56) * mm});
            skFitSpline(sketch, "E662", {"points": [v(13.1, 44.75) * mm, v(12.55, 41.98) * mm, v(11.35, 40.21) * mm, v(10.55, 39.77) * mm, v(9.7, 39.88) * mm, v(9.53, 40.9) * mm, v(7.94, 42.75) * mm, v(5.33, 44.42) * mm, v(3.29, 45.09) * mm, v(2.51, 46.16) * mm, v(2.32, 48.31) * mm, v(2.08, 53.16) * mm, v(1.24, 60.01) * mm, v(0, 65.16) * mm, v(-1.36, 67.1) * mm], "startDerivative": vector(-4.17, -37.88) * mm, "endDerivative": vector(-20.97, 23.8) * mm});
            skFitSpline(sketch, "E663", {"points": [v(-11.16, 30.28) * mm, v(-12.37, 24.08) * mm, v(-12.4, 17.12) * mm, v(-11.05, 10.04) * mm, v(-7.92, 4) * mm], "startDerivative": vector(-6.1, -25.35) * mm, "endDerivative": vector(14.18, -23.35) * mm});
            skLineSegment(sketch, "E664", {"start": v(-7.92, 4) * mm, "end": v(-7.25, 5.47) * mm});
            skLineSegment(sketch, "E665", {"start": v(-7.25, 5.47) * mm, "end": v(-7.98, 6.69) * mm});
            skLineSegment(sketch, "E666", {"start": v(-7.98, 6.69) * mm, "end": v(-7.4, 7.39) * mm});
            skLineSegment(sketch, "E667", {"start": v(-7.4, 7.39) * mm, "end": v(-9.17, 10.26) * mm});
            skLineSegment(sketch, "E668", {"start": v(-9.17, 10.26) * mm, "end": v(-9.7, 11.02) * mm});
            skLineSegment(sketch, "E669", {"start": v(-9.7, 11.02) * mm, "end": v(-9.1, 12.35) * mm});
            skLineSegment(sketch, "E670", {"start": v(-9.1, 12.35) * mm, "end": v(-9.1, 13.55) * mm});
            skLineSegment(sketch, "E671", {"start": v(-9.1, 13.55) * mm, "end": v(-8, 13.83) * mm});
            skFitSpline(sketch, "E672", {"points": [v(-8, 13.83) * mm, v(-10.21, 18.82) * mm, v(-11.24, 24.24) * mm, v(-11.16, 30.28) * mm], "startDerivative": vector(-7.5, 15.02) * mm, "endDerivative": vector(0.92, 17.77) * mm});
            skPoint(sketch, "E673.0.internal.orphan", {"position": v(0, 11.63) * mm});
            skLineSegment(sketch, "E674", {"start": v(0, 11.63) * mm, "end": v(-0.57, 10.82) * mm});
            skLineSegment(sketch, "E675", {"start": v(-0.57, 10.82) * mm, "end": v(-0.5, 9.86) * mm});
            skLineSegment(sketch, "E676", {"start": v(-0.5, 9.86) * mm, "end": v(-0.13, 9.39) * mm});
            skLineSegment(sketch, "E677", {"start": v(-0.13, 9.39) * mm, "end": v(0.1, 7.35) * mm});
            skLineSegment(sketch, "E678", {"start": v(0.1, 7.35) * mm, "end": v(-0.88, 6.58) * mm});
            skLineSegment(sketch, "E679", {"start": v(-0.88, 6.58) * mm, "end": v(2.92, 1.58) * mm});
            skLineSegment(sketch, "E680", {"start": v(2.92, 1.58) * mm, "end": v(4.95, 3.6) * mm});
            skLineSegment(sketch, "E681", {"start": v(4.95, 3.6) * mm, "end": v(5.5, 3.52) * mm});
            skLineSegment(sketch, "E682", {"start": v(5.5, 3.52) * mm, "end": v(0, 11.63) * mm});
            skLineSegment(sketch, "E683", {"start": v(4.77, 9.38) * mm, "end": v(7.04, 4.43) * mm});
            skLineSegment(sketch, "E684", {"start": v(7.04, 4.43) * mm, "end": v(8.15, 4.87) * mm});
            skLineSegment(sketch, "E685", {"start": v(8.15, 4.87) * mm, "end": v(5.7, 8.9) * mm});
            skLineSegment(sketch, "E686", {"start": v(5.7, 8.9) * mm, "end": v(4.87, 9.9) * mm});
            skLineSegment(sketch, "E687", {"start": v(4.87, 9.9) * mm, "end": v(4.77, 9.37) * mm});
            skLineSegment(sketch, "E688", {"start": v(4.77, 9.37) * mm, "end": v(4.77, 9.38) * mm});
            skLineSegment(sketch, "E689", {"start": v(-1.1, -1.98) * mm, "end": v(-1.1, 3.3) * mm});
            skLineSegment(sketch, "E690", {"start": v(-1.1, 3.3) * mm, "end": v(1, -0.16) * mm});
            skLineSegment(sketch, "E691", {"start": v(1, -0.16) * mm, "end": v(0.3, -0.58) * mm});
            skLineSegment(sketch, "E692", {"start": v(0.3, -0.58) * mm, "end": v(-0.21, -0.58) * mm});
            skLineSegment(sketch, "E693", {"start": v(-0.21, -0.58) * mm, "end": v(-0.63, -1.36) * mm});
            skLineSegment(sketch, "E694", {"start": v(-0.63, -1.36) * mm, "end": v(-0.5, -1.5) * mm});
            skLineSegment(sketch, "E695", {"start": v(-0.5, -1.5) * mm, "end": v(-1.1, -1.98) * mm});
            skLineSegment(sketch, "E696", {"start": v(-6.8, 41.52) * mm, "end": v(-6.78, 41.52) * mm});
            skLineSegment(sketch, "E697", {"start": v(-10, -12.17) * mm, "end": v(-10.7, -12.64) * mm});
            skLineSegment(sketch, "E698", {"start": v(-10.7, -12.64) * mm, "end": v(-11.28, -12.68) * mm});
            skLineSegment(sketch, "E699", {"start": v(-11.28, -12.68) * mm, "end": v(-11.72, -13.67) * mm});
            skLineSegment(sketch, "E700", {"start": v(-11.72, -13.67) * mm, "end": v(-12.64, -13.55) * mm});
            skLineSegment(sketch, "E701", {"start": v(-12.64, -13.55) * mm, "end": v(-13.1, -13.98) * mm});
            skLineSegment(sketch, "E702", {"start": v(-13.1, -13.98) * mm, "end": v(-13.67, -13.95) * mm});
            skFitSpline(sketch, "E703", {"points": [v(-10, -12.17) * mm, v(-9.63, -12.49) * mm, v(-10.6, -16.56) * mm, v(-10.92, -22.3) * mm, v(-8.7, -31) * mm, v(-1.62, -41.63) * mm, v(-0.5, -42.9) * mm, v(0.39, -43.79) * mm, v(0.83, -43.98) * mm, v(1.48, -43.94) * mm, v(1.82, -43.62) * mm, v(5.8, -38.51) * mm, v(8.6, -31.6) * mm, v(9.32, -29.1) * mm], "startDerivative": vector(15.66, -5.77) * mm, "endDerivative": vector(8.87, 31.49) * mm});
            skLineSegment(sketch, "E704", {"start": v(9.32, -29.1) * mm, "end": v(9.48, -27.86) * mm});
            skLineSegment(sketch, "E705", {"start": v(9.48, -27.86) * mm, "end": v(10.2, -28.33) * mm});
            skLineSegment(sketch, "E706", {"start": v(10.2, -28.33) * mm, "end": v(10, -29.34) * mm});
            skLineSegment(sketch, "E707", {"start": v(10, -29.34) * mm, "end": v(11.18, -30.18) * mm});
            skLineSegment(sketch, "E708", {"start": v(11.18, -30.18) * mm, "end": v(11.7, -30.02) * mm});
            skLineSegment(sketch, "E709", {"start": v(11.7, -30.02) * mm, "end": v(11.81, -30.44) * mm});
            skLineSegment(sketch, "E710", {"start": v(11.81, -30.44) * mm, "end": v(12.18, -31.05) * mm});
            skLineSegment(sketch, "E711", {"start": v(12.18, -31.05) * mm, "end": v(13.3, -31.05) * mm});
            skLineSegment(sketch, "E712", {"start": v(13.3, -31.05) * mm, "end": v(14.02, -32.75) * mm});
            skLineSegment(sketch, "E713", {"start": v(14.02, -32.75) * mm, "end": v(14.61, -33.44) * mm});
            skLineSegment(sketch, "E714", {"start": v(14.61, -33.44) * mm, "end": v(15.3, -33.53) * mm});
            skLineSegment(sketch, "E715", {"start": v(15.3, -33.53) * mm, "end": v(15.07, -40.71) * mm});
            skLineSegment(sketch, "E716", {"start": v(15.07, -40.71) * mm, "end": v(14.76, -35.66) * mm});
            skLineSegment(sketch, "E717", {"start": v(14.76, -35.66) * mm, "end": v(14.3, -35.28) * mm});
            skLineSegment(sketch, "E718", {"start": v(14.3, -35.28) * mm, "end": v(14.3, -33.57) * mm});
            skLineSegment(sketch, "E719", {"start": v(14.3, -33.57) * mm, "end": v(13.44, -32.97) * mm});
            skLineSegment(sketch, "E720", {"start": v(13.44, -32.97) * mm, "end": v(13.37, -31.83) * mm});
            skLineSegment(sketch, "E721", {"start": v(13.37, -31.83) * mm, "end": v(12.76, -31.78) * mm});
            skLineSegment(sketch, "E722", {"start": v(12.76, -31.78) * mm, "end": v(12.27, -33.8) * mm});
            skLineSegment(sketch, "E723", {"start": v(12.27, -33.8) * mm, "end": v(10.72, -37.16) * mm});
            skFitSpline(sketch, "E724", {"points": [v(10.72, -37.16) * mm, v(10.95, -40.64) * mm, v(9.6, -47.46) * mm, v(8.58, -48.87) * mm], "startDerivative": vector(1.46, -9.22) * mm, "endDerivative": vector(-4.61, -4.34) * mm});
            skFitSpline(sketch, "E725", {"points": [v(8.58, -48.87) * mm, v(9.31, -44.62) * mm, v(8.93, -42.94) * mm, v(8.52, -42.2) * mm, v(8.22, -42.15) * mm, v(8.1, -42.16) * mm, v(7.96, -42.16) * mm, v(7.79, -42.23) * mm, v(7.71, -42.57) * mm, v(6.92, -43.77) * mm, v(5.06, -46.08) * mm, v(2.99, -48.45) * mm, v(3.03, -49.43) * mm, v(3.2, -51.75) * mm, v(3.37, -54.63) * mm, v(3.26, -60.66) * mm, v(3.2, -64.09) * mm, v(2.58, -69.6) * mm, v(1.9, -72.73) * mm], "startDerivative": vector(13.2, 54.35) * mm, "endDerivative": vector(-9.28, -37.47) * mm});
            skPoint(sketch, "E726.1.internal.orphan", {"position": v(1.9, -64.39) * mm});
            skFitSpline(sketch, "E727", {"points": [v(1.9, -72.73) * mm, v(1.9, -64.39) * mm, v(1.02, -55.52) * mm, v(0, -52.05) * mm, v(-0.3, -51.67) * mm, v(-0.7, -51.89) * mm, v(-1.4, -52.42) * mm, v(-4.2, -53.7) * mm, v(-9.02, -54.1) * mm], "startDerivative": vector(0.74, 39.31) * mm, "endDerivative": vector(-32.08, -0.2) * mm});
            skFitSpline(sketch, "E728", {"points": [v(-9.02, -54.1) * mm, v(-5.85, -52.62) * mm, v(-3.08, -49.79) * mm, v(-2.23, -48.63) * mm, v(-2.22, -48) * mm, v(-4.02, -46.08) * mm, v(-6.53, -43.05) * mm, v(-9.74, -37.94) * mm, v(-12.64, -31.89) * mm, v(-13.55, -30) * mm, v(-13.86, -29.42) * mm, v(-14.32, -29.42) * mm, v(-14.67, -30.87) * mm, v(-15, -34.05) * mm, v(-14.93, -37.03) * mm, v(-14.76, -38.6) * mm, v(-15.75, -34.75) * mm, v(-15.96, -30.66) * mm, v(-15.9, -25.82) * mm, v(-15.22, -19.23) * mm, v(-14.2, -15.85) * mm, v(-13.67, -13.95) * mm], "startDerivative": vector(61.27, 21.2) * mm, "endDerivative": vector(12, 45.98) * mm});
            skFitSpline(sketch, "E729", {"points": [v(1.63, -39.2) * mm, v(0.4, -37.26) * mm, v(0, -34.92) * mm, v(0, -34.52) * mm, v(-0.07, -34.22) * mm, v(0.03, -33.95) * mm, v(0.29, -33.78) * mm, v(1.7, -32.59) * mm, v(3.41, -29.6) * mm, v(4.37, -26.4) * mm, v(4.76, -24.66) * mm, v(4.77, -24) * mm], "startDerivative": vector(-11.68, 14.08) * mm, "endDerivative": vector(-0.32, 9.2) * mm});
            skLineSegment(sketch, "E730", {"start": v(4.77, -24) * mm, "end": v(3.94, -24) * mm});
            skLineSegment(sketch, "E731", {"start": v(3.94, -24) * mm, "end": v(3.35, -23.6) * mm});
            skLineSegment(sketch, "E732", {"start": v(3.35, -23.6) * mm, "end": v(2.88, -23.53) * mm});
            skLineSegment(sketch, "E733", {"start": v(2.88, -23.53) * mm, "end": v(2.46, -23.15) * mm});
            skLineSegment(sketch, "E734", {"start": v(2.46, -23.15) * mm, "end": v(2.53, -21.9) * mm});
            skLineSegment(sketch, "E735", {"start": v(2.53, -21.9) * mm, "end": v(2.88, -21.62) * mm});
            skLineSegment(sketch, "E736", {"start": v(2.88, -21.62) * mm, "end": v(3.43, -21.55) * mm});
            skLineSegment(sketch, "E737", {"start": v(3.43, -21.55) * mm, "end": v(2.72, -21.16) * mm});
            skLineSegment(sketch, "E738", {"start": v(2.72, -21.16) * mm, "end": v(1.92, -20.48) * mm});
            skLineSegment(sketch, "E739", {"start": v(1.92, -20.48) * mm, "end": v(1.95, -19.9) * mm});
            skLineSegment(sketch, "E740", {"start": v(1.95, -19.9) * mm, "end": v(1.66, -19.68) * mm});
            skFitSpline(sketch, "E741", {"points": [v(1.66, -19.68) * mm, v(1.24, -22.35) * mm, v(0.26, -24.63) * mm, v(-1.65, -26.46) * mm], "startDerivative": vector(-0.93, -7.98) * mm, "endDerivative": vector(-6.32, -5.07) * mm});
            skLineSegment(sketch, "E742", {"start": v(-1.65, -26.46) * mm, "end": v(-1.06, -27.14) * mm});
            skLineSegment(sketch, "E743", {"start": v(-1.06, -27.14) * mm, "end": v(-1.05, -28.88) * mm});
            skLineSegment(sketch, "E744", {"start": v(-1.05, -28.88) * mm, "end": v(-1.64, -29.4) * mm});
            skLineSegment(sketch, "E745", {"start": v(-1.64, -29.4) * mm, "end": v(-1.62, -30.54) * mm});
            skLineSegment(sketch, "E746", {"start": v(-1.62, -30.54) * mm, "end": v(-2.65, -31.64) * mm});
            skLineSegment(sketch, "E747", {"start": v(-2.65, -31.64) * mm, "end": v(-2.47, -32.49) * mm});
            skFitSpline(sketch, "E748", {"points": [v(-2.47, -32.49) * mm, v(-3.3, -32.85) * mm, v(-3.48, -33.07) * mm, v(-3.5, -33.43) * mm, v(-2.47, -34.1) * mm, v(-2.03, -35.03) * mm, v(-1.51, -36.46) * mm, v(-0.5, -37.76) * mm, v(1.63, -39.2) * mm], "startDerivative": vector(-8.52, -3.34) * mm, "endDerivative": vector(12.17, -7.28) * mm});
            skLineSegment(sketch, "E749", {"start": v(4.8, -13.83) * mm, "end": v(4.8, -11.12) * mm});
            skLineSegment(sketch, "E750", {"start": v(4.8, -11.12) * mm, "end": v(3.7, -7.04) * mm});
            skLineSegment(sketch, "E751", {"start": v(3.7, -7.04) * mm, "end": v(2.08, -8.63) * mm});
            skLineSegment(sketch, "E752", {"start": v(2.08, -8.63) * mm, "end": v(2.22, -9.28) * mm});
            skLineSegment(sketch, "E753", {"start": v(2.22, -9.28) * mm, "end": v(1.87, -9.56) * mm});
            skLineSegment(sketch, "E754", {"start": v(1.87, -9.56) * mm, "end": v(2.33, -10.1) * mm});
            skLineSegment(sketch, "E755", {"start": v(2.33, -10.1) * mm, "end": v(2.2, -11.01) * mm});
            skLineSegment(sketch, "E756", {"start": v(2.2, -11.01) * mm, "end": v(2.51, -11.04) * mm});
            skLineSegment(sketch, "E757", {"start": v(2.51, -11.04) * mm, "end": v(2.58, -11.6) * mm});
            skLineSegment(sketch, "E758", {"start": v(2.58, -11.6) * mm, "end": v(4.31, -12.92) * mm});
            skLineSegment(sketch, "E759", {"start": v(4.31, -12.92) * mm, "end": v(4.8, -13.83) * mm});
            skLineSegment(sketch, "E760", {"start": v(7.16, -10.9) * mm, "end": v(7.8, -11.07) * mm});
            skLineSegment(sketch, "E761", {"start": v(7.8, -11.07) * mm, "end": v(7.74, -10.53) * mm});
            skLineSegment(sketch, "E762", {"start": v(7.74, -10.53) * mm, "end": v(8.39, -10.39) * mm});
            skLineSegment(sketch, "E763", {"start": v(8.39, -10.39) * mm, "end": v(8.12, -8.13) * mm});
            skLineSegment(sketch, "E764", {"start": v(8.12, -8.13) * mm, "end": v(7.71, -8.01) * mm});
            skLineSegment(sketch, "E765", {"start": v(7.71, -8.01) * mm, "end": v(7.79, -6.99) * mm});
            skLineSegment(sketch, "E766", {"start": v(7.79, -6.99) * mm, "end": v(7.41, -6.96) * mm});
            skLineSegment(sketch, "E767", {"start": v(7.41, -6.96) * mm, "end": v(7.27, -5.3) * mm});
            skLineSegment(sketch, "E768", {"start": v(7.27, -5.3) * mm, "end": v(7.77, -4.91) * mm});
            skLineSegment(sketch, "E769", {"start": v(7.77, -4.91) * mm, "end": v(7.79, -3.84) * mm});
            skLineSegment(sketch, "E770", {"start": v(7.79, -3.84) * mm, "end": v(7.6, -3.8) * mm});
            skLineSegment(sketch, "E771", {"start": v(7.6, -3.8) * mm, "end": v(7.62, -2.83) * mm});
            skLineSegment(sketch, "E772", {"start": v(7.62, -2.83) * mm, "end": v(7.35, -2.92) * mm});
            skLineSegment(sketch, "E773", {"start": v(7.35, -2.92) * mm, "end": v(7.38, -3.94) * mm});
            skLineSegment(sketch, "E774", {"start": v(7.38, -3.94) * mm, "end": v(7.17, -4.65) * mm});
            skLineSegment(sketch, "E775", {"start": v(7.17, -4.65) * mm, "end": v(5.65, -5.61) * mm});
            skLineSegment(sketch, "E776", {"start": v(5.65, -5.61) * mm, "end": v(5.97, -5.76) * mm});
            skLineSegment(sketch, "E777", {"start": v(5.97, -5.76) * mm, "end": v(6.28, -7.8) * mm});
            skLineSegment(sketch, "E778", {"start": v(6.28, -7.8) * mm, "end": v(7, -8.04) * mm});
            skLineSegment(sketch, "E779", {"start": v(7, -8.04) * mm, "end": v(6.58, -9) * mm});
            skLineSegment(sketch, "E780", {"start": v(6.58, -9) * mm, "end": v(7.08, -9.55) * mm});
            skLineSegment(sketch, "E781", {"start": v(7.08, -9.55) * mm, "end": v(6.5, -10.06) * mm});
            skLineSegment(sketch, "E782", {"start": v(6.5, -10.06) * mm, "end": v(7.1, -10.33) * mm});
            skLineSegment(sketch, "E783", {"start": v(7.1, -10.33) * mm, "end": v(7.16, -10.9) * mm});
            skSolve(sketch);
        }
        {
            var Q0;
            Q0 = qSketchRegion(id + "F0", true);
            extrude(context, id + "F1", {"entities" : qUnion([Q0]), "depth" : 25.4 * mm, "offsetDistance" : 25.4 * mm});
        }
        {
            var Q0;
            Q0=qCreatedBy(makeId("Top.planeOp"),FACE);
            var sketch = newSketch(context, id + "F2", { "sketchPlane" : qUnion([Q0])});
            skLineSegment(sketch, "E784.bottom", {"start": v(-76.18, 76.22) * mm, "end": v(76.42, 76.22) * mm});
            skLineSegment(sketch, "E784.top", {"start": v(-76.18, -76.21) * mm, "end": v(76.42, -76.21) * mm});
            skLineSegment(sketch, "E784.left", {"start": v(-76.18, 76.22) * mm, "end": v(-76.18, -76.21) * mm});
            skLineSegment(sketch, "E784.right", {"start": v(76.42, 76.22) * mm, "end": v(76.42, -76.21) * mm});
            skSolve(sketch);
        }
        {
            var Q0;
            Q0 = qSketchRegion(id + "F2", true);
            extrude(context, id + "F3", {"entities" : qUnion([Q0]), "depth" : 19.05 * mm, "offsetDistance" : 25.4 * mm});
        }
    });
